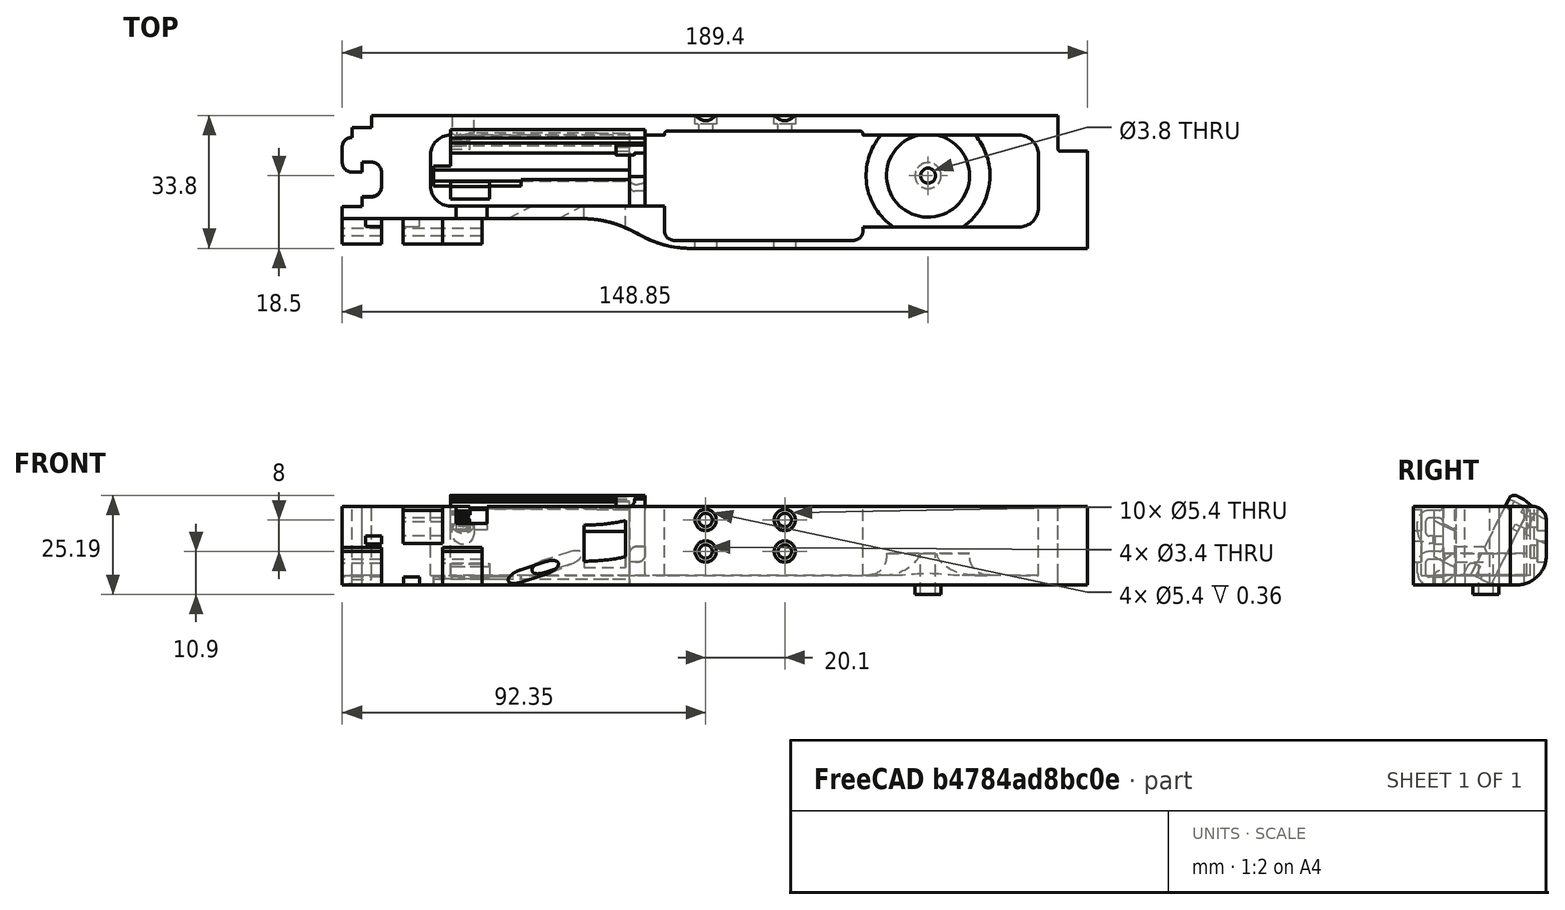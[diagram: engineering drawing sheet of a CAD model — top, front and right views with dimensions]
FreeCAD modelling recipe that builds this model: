
FCSTD DOCUMENT  (FreeCAD 0.19R0.19.2)
Label: rightSideV1_0
License: All rights reserved
LicenseURL: http://en.wikipedia.org/wiki/All_rights_reserved
objects: Sketcher::SketchObject×44, Part::Extrusion×35, Part::MultiFuse×23, Part::Box×18, Part::Cut×15, Part::Fillet×13, App::MeasureDistance×10, Part::Cylinder×4, Part::Revolution×1, Mesh::Feature×1
note: 153 computed .brp shape members not serialized (recipe doc carries the construction recipe); baked Part::Feature solids carry a one-line shape summary decoded from their .brp

FEATURE [Sketcher::SketchObject] Sketch
  FullyConstrained = true
  sketch-geometry (36):
    g0: LineSegment StartX=0 StartY=0 StartZ=0 EndX=154.4 EndY=0 EndZ=0
    g1: LineSegment StartX=154.4 StartY=0 StartZ=0 EndX=154.4 EndY=-7.6 EndZ=0
    g2: LineSegment StartX=32.5209 StartY=-26.2 StartZ=0 EndX=-7.5 EndY=-26.2 EndZ=0
    g3-g7: Circle x5 (B-spline internal-alignment scaffolding for g8; pole/knot coordinates omitted)
    g8: BSplineCurve PolesCount=5 KnotsCount=3 Degree=3 IsPeriodic=0
    g9: GeomPoint X=61.85 Y=-33.8 Z=0
    g10: GeomPoint X=47.185 Y=-29.9 Z=0
    g11: GeomPoint X=32.5209 Y=-26.2 Z=0
    g12: Circle CenterX=121.35 CenterY=-14.3 CenterZ=0 NormalX=0 NormalY=0 NormalZ=1 AngleXU=0 Radius=3.25
    g13: LineSegment StartX=-7.5 StartY=-26.2 StartZ=0 EndX=-27.5 EndY=-26.2 EndZ=0
    g14: LineSegment StartX=-20 StartY=0 StartZ=0 EndX=0 EndY=0 EndZ=0
    g15: LineSegment StartX=-25 StartY=-3.1 StartZ=0 EndX=-20 EndY=-3.1 EndZ=0
    g16: LineSegment StartX=-25 StartY=-3.1 StartZ=0 EndX=-25 EndY=-5.6 EndZ=0
    g17: LineSegment StartX=-27.5 StartY=-8.1 StartZ=0 EndX=-27.5 EndY=-11.85 EndZ=0
    g18: ArcOfCircle CenterX=-25 CenterY=-8.1 CenterZ=0 NormalX=0 NormalY=0 NormalZ=1 AngleXU=0 Radius=2.5 StartAngle=1.5708 EndAngle=3.14159
    g19: LineSegment StartX=-25 StartY=-14.35 StartZ=0 EndX=-22.5 EndY=-14.35 EndZ=0
    g20: ArcOfCircle CenterX=-25 CenterY=-11.85 CenterZ=0 NormalX=0 NormalY=0 NormalZ=1 AngleXU=0 Radius=2.5 StartAngle=3.14159 EndAngle=4.71239
    g21: LineSegment StartX=-22.5 StartY=-14.35 StartZ=0 EndX=-22.5 EndY=-11.85 EndZ=0
    g22: LineSegment StartX=-22.5 StartY=-11.85 StartZ=0 EndX=-20 EndY=-11.85 EndZ=0
    g23: ArcOfCircle CenterX=-20 CenterY=-14.35 CenterZ=0 NormalX=0 NormalY=0 NormalZ=1 AngleXU=0 Radius=2.5 StartAngle=8e-16 EndAngle=1.5708
    g24: LineSegment StartX=-17.5 StartY=-14.35 StartZ=0 EndX=-17.5 EndY=-18.1 EndZ=0
    g25: ArcOfCircle CenterX=-20 CenterY=-18.1 CenterZ=0 NormalX=0 NormalY=0 NormalZ=1 AngleXU=0 Radius=2.5 StartAngle=4.71239 EndAngle=6.28319
    g26: LineSegment StartX=-22.5 StartY=-20.6 StartZ=0 EndX=-20 EndY=-20.6 EndZ=0
    g27: LineSegment StartX=-22.5 StartY=-20.6 StartZ=0 EndX=-22.5 EndY=-23.1 EndZ=0
    g28: LineSegment StartX=-27.5 StartY=-23.1 StartZ=0 EndX=-22.5 EndY=-23.1 EndZ=0
    g29: LineSegment StartX=-20 StartY=-3.1 StartZ=0 EndX=-20 EndY=0 EndZ=0
    g30: LineSegment StartX=-27.5 StartY=-23.1 StartZ=0 EndX=-27.5 EndY=-26.2 EndZ=0
    g31: LineSegment StartX=154.4 StartY=-7.6 StartZ=0 EndX=154.4 EndY=-8.6 EndZ=0
    g32: ArcOfCircle CenterX=154.9 CenterY=-8.6 CenterZ=0 NormalX=0 NormalY=0 NormalZ=1 AngleXU=0 Radius=0.5 StartAngle=3.14159 EndAngle=4.71239
    g33: LineSegment StartX=154.9 StartY=-9.1 StartZ=0 EndX=161.9 EndY=-9.1 EndZ=0
    g34: LineSegment StartX=161.9 StartY=-9.1 StartZ=0 EndX=161.9 EndY=-33.8 EndZ=0
    g35: LineSegment StartX=161.9 StartY=-33.8 StartZ=0 EndX=61.85 EndY=-33.8 EndZ=0
  constraints (72):
    c: PointOnObject(g0,g-2)
    c: Horizontal(g0)
    c: Distance(g0) = 154.4
    c: DistanceY(g-1,g0) = 0
    c: Vertical(g1)
    c: Distance(g1) = 7.6
    c: Coincident(g1,g0)
    c: Horizontal(g2)
    c: Block(g2)
    c: Weight(g3) = 1
    c: Coincident(g8,g2)
    c: InternalAlignment(g3-g7 -> g8) x5
    c: InternalAlignment(g9,g8)
    c: InternalAlignment(g10,g8)
    c: InternalAlignment(g11,g8)
    c: Block(g12)
    c: Coincident(g13,g2)
    c: Horizontal(g13)
    c: Distance(g13) = 20
    c: Horizontal(g14)
    c: Distance(g14) = 20
    c: Coincident(g14,g0)
    c: Horizontal(g15)
    c: Vertical(g16)
    c: Coincident(g16,g15)
    c: Vertical(g17)
    c: Coincident(g18,g16)
    c: Block(g18)
    c: Coincident(g17,g18)
    c: Horizontal(g19)
    c: Coincident(g20,g17)
    c: Block(g20)
    c: Block(g19)
    c: Vertical(g21)
    c: Coincident(g21,g19)
    c: Horizontal(g22)
    c: Coincident(g22,g21)
    c: Coincident(g23,g22)
    c: Vertical(g24)
    c: Block(g23)
    c: Coincident(g24,g23)
    c: Coincident(g25,g24)
    c: Block(g25)
    c: Horizontal(g26)
    c: Coincident(g26,g25)
    c: Vertical(g27)
    c: Coincident(g27,g26)
    c: Horizontal(g28)
    c: Coincident(g28,g27)
    c: Block(g15)
    c: Block(g28)
    c: Coincident(g29,g15)
    c: Coincident(g29,g14)
    c: Vertical(g29)
    c: Coincident(g30,g28)
    c: Coincident(g30,g13)
    c: Vertical(g30)
    c: Vertical(g31)
    c: Distance(g31) = 1
    c: Coincident(g31,g1)
    c: Coincident(g32,g31)
    c: Block(g32)
    c: Coincident(g33,g32)
    c: Horizontal(g33)
    c: Coincident(g34,g33)
    c: Vertical(g34)
    c: Block(g34)
    c: Coincident(g35,g34)
    c: Horizontal(g35)
    c: Block(g35)
    c: Coincident(g8,g35)
    c: Block(g8)
FEATURE [Part::Extrusion] Extrude  label="mainBodyBaseExtrude"
  Base = -> Sketch
  Dir = (0,0,1)
  DirMode = 2
  FaceMakerClass = Part::FaceMakerBullseye
  LengthFwd = 2.4
  LengthRev = 0
  Solid = true
  Symmetric = false
FEATURE [Sketcher::SketchObject] Sketch001
  FullyConstrained = true
  sketch-geometry (75):
    g0: ArcOfCircle CenterX=144.4 CenterY=-10 CenterZ=0 NormalX=0 NormalY=0 NormalZ=1 AngleXU=0 Radius=5 StartAngle=4.345e-13 EndAngle=1.5708
    g1: LineSegment StartX=32.5209 StartY=-26.2 StartZ=0 EndX=-7.49911 EndY=-26.2 EndZ=0
    g2: LineSegment StartX=0 StartY=0 StartZ=0 EndX=154.4 EndY=0 EndZ=0
    g3-g7: Circle x5 (B-spline internal-alignment scaffolding for g8; pole/knot coordinates omitted)
    g8: BSplineCurve PolesCount=5 KnotsCount=3 Degree=3 IsPeriodic=0
    g9: GeomPoint X=61.85 Y=-33.8 Z=0
    g10: GeomPoint X=47.1857 Y=-29.9 Z=0
    g11: GeomPoint X=32.5209 Y=-26.2 Z=0
    g12: LineSegment StartX=154.4 StartY=0 StartZ=0 EndX=154.4 EndY=-7.6 EndZ=0
    g13: LineSegment StartX=20 StartY=-5 StartZ=0 EndX=54.35 EndY=-5 EndZ=0
    g14: LineSegment StartX=104.85 StartY=-5 StartZ=0 EndX=144.4 EndY=-5 EndZ=0
    g15: LineSegment StartX=54.35 StartY=-23 StartZ=0 EndX=20 EndY=-23 EndZ=0
    g16: LineSegment StartX=-27.4991 StartY=-26.2 StartZ=0 EndX=-7.49911 EndY=-26.2 EndZ=0
    g17: LineSegment StartX=-20 StartY=0 StartZ=0 EndX=0 EndY=0 EndZ=0
    g18: LineSegment StartX=-27.4991 StartY=-23.2 StartZ=0 EndX=-22.5 EndY=-23.2 EndZ=0
    g19: LineSegment StartX=-22.5 StartY=-20.7 StartZ=0 EndX=-22.5 EndY=-23.2 EndZ=0
    g20: LineSegment StartX=-22.5 StartY=-20.7 StartZ=0 EndX=-20 EndY=-20.7 EndZ=0
    g21: ArcOfCircle CenterX=-20 CenterY=-18.2 CenterZ=0 NormalX=0 NormalY=0 NormalZ=1 AngleXU=0 Radius=2.5 StartAngle=4.71239 EndAngle=6.28319
    g22: LineSegment StartX=-17.5 StartY=-14.4 StartZ=0 EndX=-17.5 EndY=-18.2 EndZ=0
    g23: ArcOfCircle CenterX=-20 CenterY=-14.4 CenterZ=0 NormalX=0 NormalY=0 NormalZ=1 AngleXU=0 Radius=2.5 StartAngle=9e-16 EndAngle=1.5708
    g24: LineSegment StartX=-22.5 StartY=-11.9 StartZ=0 EndX=-20 EndY=-11.9 EndZ=0
    g25: LineSegment StartX=-22.5 StartY=-14.4 StartZ=0 EndX=-22.5 EndY=-11.9 EndZ=0
    g26: LineSegment StartX=-25 StartY=-14.4 StartZ=0 EndX=-22.5 EndY=-14.4 EndZ=0
    g27: ArcOfCircle CenterX=-25 CenterY=-11.9 CenterZ=0 NormalX=0 NormalY=0 NormalZ=1 AngleXU=0 Radius=2.5 StartAngle=3.14159 EndAngle=4.71239
    g28: LineSegment StartX=-27.5 StartY=-8.1 StartZ=0 EndX=-27.5 EndY=-11.9 EndZ=0
    g29: ArcOfCircle CenterX=-25 CenterY=-8.1 CenterZ=0 NormalX=0 NormalY=0 NormalZ=1 AngleXU=0 Radius=2.5 StartAngle=1.5708 EndAngle=3.14159
    g30: LineSegment StartX=-25 StartY=-3.1 StartZ=0 EndX=-25 EndY=-5.6 EndZ=0
    g31: LineSegment StartX=-20 StartY=-3.1 StartZ=0 EndX=-25 EndY=-3.1 EndZ=0
    g32: LineSegment StartX=-20 StartY=0 StartZ=0 EndX=-20 EndY=-3.1 EndZ=0
    g33: LineSegment StartX=-27.4991 StartY=-26.2 StartZ=0 EndX=-27.4991 EndY=-23.2 EndZ=0
    g34: LineSegment StartX=4.09e-14 StartY=-5 StartZ=0 EndX=20 EndY=-5 EndZ=0
    g35: ArcOfCircle CenterX=7.1e-15 CenterY=-18 CenterZ=0 NormalX=0 NormalY=0 NormalZ=1 AngleXU=0 Radius=5 StartAngle=3.14159 EndAngle=4.71239
    g36: ArcOfCircle CenterX=4.26e-14 CenterY=-10 CenterZ=0 NormalX=0 NormalY=0 NormalZ=1 AngleXU=0 Radius=5 StartAngle=1.5708 EndAngle=3.14159
    g37: LineSegment StartX=-5 StartY=-18 StartZ=0 EndX=-5 EndY=-10 EndZ=0
    g38: LineSegment StartX=6.2e-15 StartY=-23 StartZ=0 EndX=20 EndY=-23 EndZ=0
    g39: LineSegment StartX=154.4 StartY=-7.6 StartZ=0 EndX=154.4 EndY=-8.6 EndZ=0
    g40: LineSegment StartX=154.9 StartY=-9.1 StartZ=0 EndX=161.9 EndY=-9.1 EndZ=0
    g41: ArcOfCircle CenterX=154.9 CenterY=-8.6 CenterZ=0 NormalX=0 NormalY=0 NormalZ=1 AngleXU=0 Radius=0.5 StartAngle=3.14159 EndAngle=4.71299
    g42: LineSegment StartX=104.85 StartY=-28.3916 StartZ=0 EndX=144.408 EndY=-28.3916 EndZ=0
    g43: LineSegment StartX=149.4 StartY=-10 StartZ=0 EndX=149.4 EndY=-23.4 EndZ=0
    g44: ArcOfCircle CenterX=144.408 CenterY=-23.4 CenterZ=0 NormalX=0 NormalY=0 NormalZ=1 AngleXU=0 Radius=4.99164 StartAngle=4.71239 EndAngle=6.28319
    g45: LineSegment StartX=104.85 StartY=-28.3916 StartZ=0 EndX=104.85 EndY=-28.7833 EndZ=0
    g46: LineSegment StartX=54.35 StartY=-28.7916 StartZ=0 EndX=54.35 EndY=-23 EndZ=0
    g47: LineSegment StartX=161.9 StartY=-33.8 StartZ=0 EndX=161.9 EndY=-9.1 EndZ=0
    g48: LineSegment StartX=61.85 StartY=-33.8 StartZ=0 EndX=161.9 EndY=-33.8 EndZ=0
    g49: Circle CenterX=54.35 CenterY=-28.7916 CenterZ=0 NormalX=0 NormalY=0 NormalZ=1 AngleXU=0 Radius=1
    g50: Circle CenterX=54.35 CenterY=-31.7916 CenterZ=0 NormalX=0 NormalY=0 NormalZ=1 AngleXU=0 Radius=1
    g51: Circle CenterX=57.35 CenterY=-31.7916 CenterZ=0 NormalX=0 NormalY=0 NormalZ=1 AngleXU=0 Radius=1
    g52: BSplineCurve PolesCount=3 KnotsCount=2 Degree=2 IsPeriodic=0
    g53: GeomPoint X=54.35 Y=-28.7916 Z=0
    g54: GeomPoint X=57.35 Y=-31.7916 Z=0
    g55: Circle CenterX=104.85 CenterY=-28.7833 CenterZ=0 NormalX=0 NormalY=0 NormalZ=1 AngleXU=0 Radius=1
    g56: Circle CenterX=104.85 CenterY=-31.7916 CenterZ=0 NormalX=0 NormalY=0 NormalZ=1 AngleXU=0 Radius=1
    g57: Circle CenterX=101.85 CenterY=-31.7916 CenterZ=0 NormalX=0 NormalY=0 NormalZ=1 AngleXU=0 Radius=1
    g58: BSplineCurve PolesCount=3 KnotsCount=2 Degree=2 IsPeriodic=0
    g59: GeomPoint X=104.85 Y=-28.7833 Z=0
    g60: GeomPoint X=101.85 Y=-31.7916 Z=0
    g61: LineSegment StartX=57.35 StartY=-31.7916 StartZ=0 EndX=101.85 EndY=-31.7916 EndZ=0
    g62: Circle CenterX=54.35 CenterY=-5 CenterZ=0 NormalX=0 NormalY=0 NormalZ=1 AngleXU=0 Radius=1
    g63: Circle CenterX=54.35 CenterY=-4 CenterZ=0 NormalX=0 NormalY=0 NormalZ=1 AngleXU=0 Radius=1
    g64: Circle CenterX=55.15 CenterY=-4 CenterZ=0 NormalX=0 NormalY=0 NormalZ=1 AngleXU=0 Radius=1
    g65: BSplineCurve PolesCount=3 KnotsCount=2 Degree=2 IsPeriodic=0
    g66: GeomPoint X=54.35 Y=-5 Z=0
    g67: GeomPoint X=55.15 Y=-4 Z=0
    g68: Circle CenterX=104.85 CenterY=-5 CenterZ=0 NormalX=0 NormalY=0 NormalZ=1 AngleXU=0 Radius=1
    g69: Circle CenterX=104.85 CenterY=-4 CenterZ=0 NormalX=0 NormalY=0 NormalZ=1 AngleXU=0 Radius=1
    g70: Circle CenterX=104.05 CenterY=-4 CenterZ=0 NormalX=0 NormalY=0 NormalZ=1 AngleXU=0 Radius=1
    g71: BSplineCurve PolesCount=3 KnotsCount=2 Degree=2 IsPeriodic=0
    g72: GeomPoint X=104.85 Y=-5 Z=0
    g73: GeomPoint X=104.05 Y=-4 Z=0
    g74: LineSegment StartX=104.05 StartY=-4 StartZ=0 EndX=55.15 EndY=-4 EndZ=0
  constraints (156):
    c: PointOnObject(g2,g-2)
    c: DistanceY(g-1,g2) = 0
    c: Block(g0)
    c: Horizontal(g1)
    c: Distance(g1) = 40.02
    c: Horizontal(g2)
    c: Block(g2)
    c: Weight(g3) = 1
    c: Equal(g3, g4-g7) x4
    c: Coincident(g8,g1)
    c: InternalAlignment(g3-g7 -> g8) x5
    c: InternalAlignment(g9,g8)
    c: InternalAlignment(g10,g8)
    c: InternalAlignment(g11,g8)
    c: Vertical(g12)
    c: Coincident(g12,g2)
    c: Distance(g12) = 7.6
    c: Block(g12)
    c: Horizontal(g13)
    c: Coincident(g14,g0)
    c: Horizontal(g14)
    c: Horizontal(g15)
    c: Horizontal(g16)
    c: Distance(g16) = 20
    c: Coincident(g1,g16)
    c: Horizontal(g17)
    c: Distance(g17) = 20
    c: Coincident(g17,g2)
    c: Horizontal(g31)
    c: Vertical(g30)
    c: Coincident(g29,g30)
    c: Vertical(g28)
    c: Block(g29)
    c: Coincident(g27,g28)
    c: Block(g27)
    c: Horizontal(g26)
    c: Coincident(g26,g27)
    c: Vertical(g25)
    c: Coincident(g25,g26)
    c: Horizontal(g24)
    c: Coincident(g23,g24)
    c: Block(g23)
    c: Vertical(g22)
    c: Coincident(g21,g22)
    c: Block(g21)
    c: Horizontal(g20)
    c: Coincident(g20,g21)
    c: Vertical(g19)
    c: Coincident(g19,g20)
    c: Horizontal(g18)
    c: Coincident(g18,g19)
    c: Coincident(g32,g17)
    c: Coincident(g32,g31)
    c: Vertical(g32)
    c: Coincident(g33,g16)
    c: Coincident(g33,g18)
    c: Vertical(g33)
    c: Block(g33)
    c: Block(g18)
    c: Block(g22)
    c: Block(g26)
    c: Block(g25)
    c: Block(g24)
    c: Block(g28)
    c: Block(g31)
    c: Block(g30)
    c: Horizontal(g34)
    c: Distance(g34) = 20
    c: Block(g35)
    c: Block(g36)
    c: Coincident(g37,g35)
    c: Coincident(g37,g36)
    c: Vertical(g37)
    c: Coincident(g38,g35)
    c: Coincident(g38,g15)
    c: Horizontal(g38)
    c: Block(g38)
    c: Block(g34)
    c: Block(g13)
    c: Vertical(g39)
    c: Distance(g39) = 1
    c: Coincident(g39,g12)
    c: Horizontal(g40)
    c: Coincident(g41,g39)
    c: Coincident(g41,g40)
    c: Block(g39)
    c: Block(g41)
    c: Horizontal(g42)
    c: Vertical(g43)
    c: Distance(g43) = 13.4
    c: Coincident(g43,g0)
    c: Block(g42)
    c: Block(g43)
    c: Coincident(g44,g43)
    c: Coincident(g44,g42)
    c: Block(g44)
    c: Distance(g15) = 34.35
    c: Coincident(g45,g42)
    c: Vertical(g45)
    c: Coincident(g46,g15)
    c: Vertical(g46)
    c: Coincident(g47,g40)
    c: Vertical(g47)
    c: Block(g47)
    c: Coincident(g48,g47)
    c: Horizontal(g48)
    c: Block(g48)
    c: Coincident(g8,g48)
    c: Block(g8)
    c: Coincident(g52,g46)
    c: Weight(g49) = 1
    c: Equal(g49,g50)
    c: Equal(g49,g51)
    c: InternalAlignment(g49,g52)
    c: InternalAlignment(g50,g52)
    c: InternalAlignment(g51,g52)
    c: InternalAlignment(g53,g52)
    c: InternalAlignment(g54,g52)
    c: Coincident(g58,g45)
    c: Weight(g55) = 1
    c: Equal(g55,g56)
    c: Equal(g55,g57)
    c: InternalAlignment(g55,g58)
    c: InternalAlignment(g56,g58)
    c: InternalAlignment(g57,g58)
    c: InternalAlignment(g59,g58)
    c: InternalAlignment(g60,g58)
    c: Block(g58)
    c: Block(g52)
    c: Coincident(g61,g52)
    c: Coincident(g61,g58)
    c: Horizontal(g61)
    c: Block(g14)
    c: Coincident(g65,g13)
    c: Weight(g62) = 1
    c: Equal(g62,g63)
    c: Equal(g62,g64)
    c: InternalAlignment(g62,g65)
    c: InternalAlignment(g63,g65)
    c: InternalAlignment(g64,g65)
    c: InternalAlignment(g66,g65)
    c: InternalAlignment(g67,g65)
    c: Block(g65)
    c: Coincident(g71,g14)
    c: Weight(g68) = 1
    c: Equal(g68,g69)
    c: Equal(g68,g70)
    c: InternalAlignment(g68,g71)
    c: InternalAlignment(g69,g71)
    c: InternalAlignment(g70,g71)
    c: InternalAlignment(g72,g71)
    c: InternalAlignment(g73,g71)
    c: Block(g71)
    c: Coincident(g74,g71)
    c: Coincident(g74,g65)
    c: Horizontal(g74)
FEATURE [Sketcher::SketchObject] Sketch005
  FullyConstrained = true
  Placement = pos=(0,0,0) rot=(1,0,0;1.5708rad)
  sketch-geometry (4):
    g0: Circle CenterX=84.95 CenterY=16.5 CenterZ=0 NormalX=0 NormalY=0 NormalZ=1 AngleXU=0 Radius=1.7
    g1: Circle CenterX=84.95 CenterY=8.5 CenterZ=0 NormalX=0 NormalY=0 NormalZ=1 AngleXU=0 Radius=1.7
    g2: Circle CenterX=64.85 CenterY=8.5 CenterZ=0 NormalX=0 NormalY=0 NormalZ=1 AngleXU=0 Radius=1.7
    g3: Circle CenterX=64.85 CenterY=16.5 CenterZ=0 NormalX=0 NormalY=0 NormalZ=1 AngleXU=0 Radius=1.7
  constraints (4):
    c: Block(g0)
    c: Block(g1)
    c: Block(g2)
    c: Block(g3)
FEATURE [Part::Extrusion] Extrude004  label="removeFromMainBodyToCreateScrewHolesForSolenoidExtrude004"
  Base = -> Sketch005
  Dir = (0,-1,1.1e-15)
  DirMode = 2
  FaceMakerClass = Part::FaceMakerBullseye
  LengthFwd = 10
  LengthRev = 0
  Solid = true
  Symmetric = false
FEATURE [Sketcher::SketchObject] Sketch004
  FullyConstrained = true
  Placement = pos=(0,0,0) rot=(1,0,0;1.5708rad)
  sketch-geometry (12):
    g0: LineSegment StartX=15.75 StartY=2.5 StartZ=0 EndX=15.75 EndY=0 EndZ=0
    g1: Circle CenterX=15.75 CenterY=2.5 CenterZ=0 NormalX=0 NormalY=0 NormalZ=1 AngleXU=0 Radius=1
    g2: Circle CenterX=10.55 CenterY=2.5 CenterZ=0 NormalX=0 NormalY=0 NormalZ=1 AngleXU=0 Radius=1
    g3: Circle CenterX=10.55 CenterY=8 CenterZ=0 NormalX=0 NormalY=0 NormalZ=1 AngleXU=0 Radius=1
    g4: BSplineCurve PolesCount=3 KnotsCount=2 Degree=2 IsPeriodic=0
    g5: GeomPoint X=15.75 Y=2.5 Z=0
    g6: GeomPoint X=10.55 Y=8 Z=0
    g7: LineSegment StartX=1.9 StartY=8 StartZ=0 EndX=10.55 EndY=8 EndZ=0
    g8: LineSegment StartX=1.9 StartY=-2.4 StartZ=0 EndX=1.9 EndY=8 EndZ=0
    g9: LineSegment StartX=3.30092 StartY=-2.4 StartZ=0 EndX=3.30092 EndY=0 EndZ=0
    g10: LineSegment StartX=15.75 StartY=0 StartZ=0 EndX=3.30092 EndY=0 EndZ=0
    g11: LineSegment StartX=3.30092 StartY=-2.4 StartZ=0 EndX=1.9 EndY=-2.4 EndZ=0
  constraints (26):
    c: Vertical(g0)
    c: Distance(g0) = 2.5
    c: Coincident(g4,g0)
    c: Weight(g1) = 1
    c: Equal(g1,g2)
    c: Equal(g1,g3)
    c: InternalAlignment(g1,g4)
    c: InternalAlignment(g2,g4)
    c: InternalAlignment(g3,g4)
    c: InternalAlignment(g5,g4)
    c: InternalAlignment(g6,g4)
    c: Block(g4)
    c: Coincident(g7,g4)
    c: Horizontal(g7)
    c: Vertical(g8)
    c: Coincident(g8,g7)
    c: Block(g8)
    c: Vertical(g9)
    c: Coincident(g10,g0)
    c: PointOnObject(g10,g-1)
    c: Horizontal(g10)
    c: Coincident(g10,g9)
    c: Block(g9)
    c: Coincident(g11,g9)
    c: Coincident(g11,g8)
    c: Horizontal(g11)
FEATURE [Sketcher::SketchObject] Sketch007
  FullyConstrained = true
  Placement = pos=(0,-14.3,2.37) rot=(-1,0,0;2.03453rad)
  sketch-geometry (6):
    g0: LineSegment StartX=0 StartY=0 StartZ=0 EndX=45.5 EndY=0 EndZ=0
    g1: LineSegment StartX=0 StartY=0 StartZ=0 EndX=0 EndY=-21.2 EndZ=0
    g2: LineSegment StartX=45.5 StartY=0 StartZ=0 EndX=49.5 EndY=0 EndZ=0
    g3: LineSegment StartX=49.5 StartY=0 StartZ=0 EndX=49.5 EndY=-21.2 EndZ=0
    g4: LineSegment StartX=49.5 StartY=-21.2 StartZ=0 EndX=0 EndY=-21.2 EndZ=0
    g5: Circle CenterX=3.25 CenterY=-18.05 CenterZ=0 NormalX=0 NormalY=0 NormalZ=1 AngleXU=0 Radius=1.6
  constraints (15):
    c: Coincident(g0,g-1)
    c: Horizontal(g0)
    c: Distance(g0) = 45.5
    c: Coincident(g1,g0)
    c: Vertical(g1)
    c: Horizontal(g2)
    c: Distance(g2) = 4
    c: Coincident(g2,g0)
    c: Coincident(g3,g2)
    c: Vertical(g3)
    c: Block(g3)
    c: Coincident(g4,g3)
    c: Horizontal(g4)
    c: Coincident(g4,g1)
    c: Block(g5)
FEATURE [Part::Extrusion] Extrude005  label="solenoidDriverHolderExtrude005"
  Base = -> Sketch007
  Dir = (0,0.894389,-0.447291)
  DirMode = 2
  FaceMakerClass = Part::FaceMakerBullseye
  LengthFwd = 10
  LengthRev = 0
  Placement = pos=(0,0,-2) rot=(0,0,1;0rad)
  Solid = true
  Symmetric = false
FEATURE [Sketcher::SketchObject] Sketch008
  FullyConstrained = false
  Placement = pos=(0,-4.3,-2.6) rot=(-1,0,0;2.03453rad)
  sketch-geometry (1):
    g0: Circle CenterX=42.25 CenterY=-3.15 CenterZ=0 NormalX=0 NormalY=0 NormalZ=1 AngleXU=0 Radius=4.5
FEATURE [Sketcher::SketchObject] Sketch009
  FullyConstrained = true
  Placement = pos=(0,-4.3,-2.6) rot=(-1,0,0;2.03453rad)
  sketch-geometry (1):
    g0: Circle CenterX=3.25 CenterY=-18.0217 CenterZ=0 NormalX=0 NormalY=0 NormalZ=1 AngleXU=0 Radius=2.8
  constraints (1):
    c: Block(g0)
FEATURE [Sketcher::SketchObject] Sketch010
  FullyConstrained = true
  Placement = pos=(0,-14.3,2.37) rot=(-1,0,0;2.03453rad)
  sketch-geometry (1):
    g0: Circle CenterX=3.25 CenterY=-18.05 CenterZ=0 NormalX=0 NormalY=0 NormalZ=1 AngleXU=0 Radius=1.6
  constraints (1):
    c: Block(g0)
FEATURE [Part::Extrusion] Extrude008  label="removeFromScrewHole3"
  Base = -> Sketch010
  Dir = (0,0.894389,-0.447291)
  DirMode = 2
  FaceMakerClass = Part::FaceMakerBullseye
  LengthFwd = -25
  LengthRev = 0
  Placement = pos=(0,4,-4) rot=(0,0,1;0rad)
  Solid = true
  Symmetric = false
FEATURE [Sketcher::SketchObject] Sketch011
  FullyConstrained = true
  Placement = pos=(0,-14.3,2.37) rot=(-1,0,0;2.03453rad)
  sketch-geometry (4):
    g0: LineSegment StartX=49.5 StartY=-21.2 StartZ=0 EndX=49.5 EndY=-22.8 EndZ=0
    g1: LineSegment StartX=49.5 StartY=-22.8 StartZ=0 EndX=0.002238 EndY=-22.8 EndZ=0
    g2: LineSegment StartX=0.002238 StartY=-21.2 StartZ=0 EndX=0.002238 EndY=-22.8 EndZ=0
    g3: LineSegment StartX=49.5 StartY=-21.2 StartZ=0 EndX=0.002238 EndY=-21.2 EndZ=0
  constraints (10):
    c: Vertical(g0)
    c: Distance(g0) = 1.6
    c: Coincident(g1,g0)
    c: Horizontal(g1)
    c: Vertical(g2)
    c: Coincident(g2,g1)
    c: Coincident(g3,g0)
    c: Coincident(g3,g2)
    c: Horizontal(g3)
    c: Block(g3)
FEATURE [Part::Extrusion] Extrude009  label="solenoidDriverTopLipFront"
  Base = -> Sketch011
  Dir = (0,0.894389,-0.447291)
  DirMode = 2
  FaceMakerClass = Part::FaceMakerBullseye
  LengthFwd = -2
  LengthRev = 0
  Placement = pos=(0,-2.9,-0.35) rot=(0,0,1;0rad)
  Solid = true
  Symmetric = false
FEATURE [Sketcher::SketchObject] Sketch012
  FullyConstrained = true
  Placement = pos=(0,-14.3,2.37) rot=(-1,0,0;2.03453rad)
  sketch-geometry (4):
    g0: LineSegment StartX=49.5 StartY=-21.2 StartZ=0 EndX=49.5 EndY=-22.8 EndZ=0
    g1: LineSegment StartX=49.5 StartY=-22.8 StartZ=0 EndX=0.002238 EndY=-22.8 EndZ=0
    g2: LineSegment StartX=0.002238 StartY=-21.2 StartZ=0 EndX=0.002238 EndY=-22.8 EndZ=0
    g3: LineSegment StartX=49.5 StartY=-21.2 StartZ=0 EndX=0.002238 EndY=-21.2 EndZ=0
  constraints (10):
    c: Vertical(g0)
    c: Distance(g0) = 1.6
    c: Coincident(g1,g0)
    c: Horizontal(g1)
    c: Vertical(g2)
    c: Coincident(g2,g1)
    c: Coincident(g3,g0)
    c: Coincident(g3,g2)
    c: Horizontal(g3)
    c: Block(g3)
FEATURE [Part::Extrusion] Extrude010  label="solenoidDriverTopLipLowerExtrude010"
  Base = -> Sketch012
  Dir = (0,0.894389,-0.447291)
  DirMode = 2
  FaceMakerClass = Part::FaceMakerBullseye
  LengthFwd = 5.05
  LengthRev = 0
  Solid = true
  Symmetric = false
FEATURE [Sketcher::SketchObject] Sketch015
  FullyConstrained = true
  Placement = pos=(0,-14.3,2.37) rot=(-1,0,0;2.03453rad)
  sketch-geometry (4):
    g0: LineSegment StartX=0 StartY=1.5 StartZ=0 EndX=0 EndY=0 EndZ=0
    g1: LineSegment StartX=0 StartY=1.5 StartZ=0 EndX=5 EndY=1.5 EndZ=0
    g2: LineSegment StartX=5 StartY=1.5 StartZ=0 EndX=5 EndY=0 EndZ=0
    g3: LineSegment StartX=0 StartY=0 StartZ=0 EndX=5 EndY=0 EndZ=0
  constraints (13):
    c: Vertical(g0)
    c: Distance(g0) = 1.5
    c: Horizontal(g1)
    c: Distance(g1) = 5
    c: Coincident(g1,g0)
    c: Vertical(g2)
    c: Distance(g2) = 1.5
    c: Coincident(g2,g1)
    c: Block(g1)
    c: Block(g2)
    c: Block(g0)
    c: Coincident(g3,g0)
    c: Coincident(g3,g2)
FEATURE [Part::Extrusion] Extrude013  label="solenoidDriverBottomLipTopExtrude012"
  Base = -> Sketch015
  Dir = (0,0.894389,-0.447291)
  DirMode = 2
  FaceMakerClass = Part::FaceMakerBullseye
  LengthFwd = -6.5
  LengthRev = 0
  Placement = pos=(0,-14.15,19.65) rot=(1,0,0;1.5708rad)
  Solid = true
  Symmetric = false
FEATURE [Sketcher::SketchObject] Sketch016
  FullyConstrained = true
  Placement = pos=(0,0,0) rot=(1,0,0;1.5708rad)
  sketch-geometry (4):
    g0: Circle CenterX=84.15 CenterY=16.5 CenterZ=0 NormalX=0 NormalY=0 NormalZ=1 AngleXU=0 Radius=2.7
    g1: Circle CenterX=64.05 CenterY=16.5 CenterZ=0 NormalX=0 NormalY=0 NormalZ=1 AngleXU=0 Radius=2.7
    g2: Circle CenterX=64.05 CenterY=8.5 CenterZ=0 NormalX=0 NormalY=0 NormalZ=1 AngleXU=0 Radius=2.7
    g3: Circle CenterX=84.15 CenterY=8.5 CenterZ=0 NormalX=0 NormalY=0 NormalZ=1 AngleXU=0 Radius=2.7
  constraints (4):
    c: Block(g0)
    c: Block(g1)
    c: Block(g3)
    c: Block(g2)
FEATURE [Part::Extrusion] Extrude014  label="removeFromMainBodyToCreateScrewHoleCounterSinks"
  Base = -> Sketch016
  Dir = (0,-1,1.1e-15)
  DirMode = 2
  FaceMakerClass = Part::FaceMakerBullseye
  LengthFwd = 1.9
  LengthRev = 0
  Placement = pos=(0.8,-0.36,0) rot=(0,0,1;0rad)
  Solid = true
  Symmetric = false
FEATURE [Part::Extrusion] Extrude015  label="removeFromScrewHole2Extrude007"
  Base = -> Sketch009
  Dir = (0,0.894389,-0.447291)
  DirMode = 2
  FaceMakerClass = Part::FaceMakerBullseye
  LengthFwd = 10
  LengthRev = 0
  Placement = pos=(0,-8,2) rot=(0,0,1;0rad)
  Solid = true
  Symmetric = false
FEATURE [Sketcher::SketchObject] Sketch017
  FullyConstrained = true
  Placement = pos=(0,-14.3,2.37) rot=(-1,0,0;2.03453rad)
  sketch-geometry (4):
    g0: LineSegment StartX=0 StartY=1.5 StartZ=0 EndX=0 EndY=0 EndZ=0
    g1: LineSegment StartX=0 StartY=1.5 StartZ=0 EndX=5 EndY=1.5 EndZ=0
    g2: LineSegment StartX=5 StartY=1.5 StartZ=0 EndX=5 EndY=0 EndZ=0
    g3: LineSegment StartX=0 StartY=0 StartZ=0 EndX=5 EndY=0 EndZ=0
  constraints (13):
    c: Vertical(g0)
    c: Distance(g0) = 1.5
    c: Horizontal(g1)
    c: Distance(g1) = 5
    c: Coincident(g1,g0)
    c: Vertical(g2)
    c: Distance(g2) = 1.5
    c: Coincident(g2,g1)
    c: Block(g1)
    c: Block(g2)
    c: Block(g0)
    c: Coincident(g3,g0)
    c: Coincident(g3,g2)
FEATURE [Part::Extrusion] Extrude016  label="solenoidDriverBottomLipTopExtrude013"
  Base = -> Sketch017
  Dir = (0,0.894389,-0.447291)
  DirMode = 2
  FaceMakerClass = Part::FaceMakerBullseye
  LengthFwd = -6.5
  LengthRev = 0
  Placement = pos=(0,-15.45,20.3) rot=(1,0,0;1.5708rad)
  Solid = true
  Symmetric = false
FEATURE [Part::Fillet] Fillet005  label="solenoidDriverBottomLipTopFillet005"
  Base = -> Extrude016
  Edges = 1 edges r=1.4: [Edge6]
FEATURE [Sketcher::SketchObject] Sketch018
  FullyConstrained = true
  Placement = pos=(38.5,-14.3,2.37) rot=(-1,0,0;2.03453rad)
  sketch-geometry (4):
    g0: LineSegment StartX=11 StartY=0 StartZ=0 EndX=11 EndY=1.5 EndZ=0
    g1: LineSegment StartX=11 StartY=0 StartZ=0 EndX=3.6 EndY=0 EndZ=0
    g2: LineSegment StartX=3.6 StartY=0 StartZ=0 EndX=3.6 EndY=1.5 EndZ=0
    g3: LineSegment StartX=11 StartY=1.5 StartZ=0 EndX=3.6 EndY=1.5 EndZ=0
  constraints (12):
    c: PointOnObject(g0,g-1)
    c: Vertical(g0)
    c: Distance(g0) = 1.5
    c: Horizontal(g1)
    c: Distance(g1) = 7.4
    c: Coincident(g1,g0)
    c: Block(g0)
    c: Coincident(g2,g1)
    c: Vertical(g2)
    c: Coincident(g3,g0)
    c: Horizontal(g3)
    c: Coincident(g2,g3)
FEATURE [Part::Extrusion] Extrude017
  Base = -> Sketch018
  Dir = (0,0.894389,-0.447291)
  DirMode = 2
  FaceMakerClass = Part::FaceMakerBullseye
  LengthFwd = 4
  LengthRev = 0
  Placement = pos=(0,-8.212,34.025) rot=(1,0,0;1.5708rad)
  Solid = true
  Symmetric = false
FEATURE [Sketcher::SketchObject] Sketch019
  FullyConstrained = true
  Placement = pos=(0,0,0) rot=(1,0,0;1.5708rad)
  sketch-geometry (4):
    g0: Circle CenterX=84.95 CenterY=8.5 CenterZ=0 NormalX=0 NormalY=0 NormalZ=1 AngleXU=0 Radius=2.7
    g1: Circle CenterX=64.85 CenterY=8.5 CenterZ=0 NormalX=0 NormalY=0 NormalZ=1 AngleXU=0 Radius=2.7
    g2: Circle CenterX=64.85 CenterY=16.5 CenterZ=0 NormalX=0 NormalY=0 NormalZ=1 AngleXU=0 Radius=2.7
    g3: Circle CenterX=84.95 CenterY=16.5 CenterZ=0 NormalX=0 NormalY=0 NormalZ=1 AngleXU=0 Radius=2.7
  constraints (4):
    c: Block(g3)
    c: Block(g2)
    c: Block(g0)
    c: Block(g1)
FEATURE [Part::Extrusion] Extrude019  label="removeSolenoidAdjusterHoles"
  Base = -> Sketch019
  Dir = (0,-1,1.1e-15)
  DirMode = 2
  FaceMakerClass = Part::FaceMakerBullseye
  LengthFwd = 6
  LengthRev = 0
  Placement = pos=(0,-30,0) rot=(0,0,1;0rad)
  Solid = true
  Symmetric = false
FEATURE [Sketcher::SketchObject] Sketch020
  FullyConstrained = true
  Placement = pos=(0,-14.3,2.37) rot=(-1,0,0;2.03453rad)
  sketch-geometry (6):
    g0: LineSegment StartX=45.5 StartY=-21.2 StartZ=0 EndX=49.5 EndY=-21.2 EndZ=0
    g1: LineSegment StartX=45.5 StartY=0 StartZ=0 EndX=49.5 EndY=0 EndZ=0
    g2: LineSegment StartX=49.5 StartY=0 StartZ=0 EndX=49.5 EndY=-21.2 EndZ=0
    g3: LineSegment StartX=4 StartY=0 StartZ=0 EndX=4 EndY=-21.2 EndZ=0
    g4: LineSegment StartX=45.5 StartY=-21.2 StartZ=0 EndX=4 EndY=-21.2 EndZ=0
    g5: LineSegment StartX=4 StartY=0 StartZ=0 EndX=45.5 EndY=0 EndZ=0
  constraints (16):
    c: Horizontal(g0)
    c: Distance(g0) = 4
    c: Horizontal(g1)
    c: Distance(g1) = 4
    c: Coincident(g2,g1)
    c: Coincident(g2,g0)
    c: Vertical(g2)
    c: Block(g2)
    c: Vertical(g3)
    c: Coincident(g4,g0)
    c: Horizontal(g4)
    c: Coincident(g4,g3)
    c: Coincident(g5,g1)
    c: Horizontal(g5)
    c: Block(g3)
    c: Block(g5)
FEATURE [Part::Box] Box  label="Cube"
  AttacherType = Attacher::AttachEngine3D
  Height = 10
  Length = 190
  Placement = pos=(-30,0,0) rot=(0,0,1;0rad)
  Width = 10
FEATURE [Part::Fillet] Fillet008
  Base = -> Box
  Edges = 1 edges r=7.5: [Edge11]
FEATURE [Part::Box] Box001  label="Cube001"
  AttacherType = Attacher::AttachEngine3D
  Height = 10
  Length = 190
  Placement = pos=(-35,0,0) rot=(0,0,1;0rad)
  Width = 10
FEATURE [Part::Cut] Cut  label="filletMain"
  Base = -> Box001
  Placement = pos=(0,-10,0) rot=(0,0,1;0rad)
  Tool = -> Fillet008
FEATURE [Part::Box] Box002  label="Cube002"
  AttacherType = Attacher::AttachEngine3D
  Height = 30
  Length = 190
  Placement = pos=(-20,0,0) rot=(0,0,1;0rad)
  Width = 10
FEATURE [Part::Box] Box003  label="Cube003"
  AttacherType = Attacher::AttachEngine3D
  Height = 10
  Length = 190
  Placement = pos=(-90,-50,-10) rot=(0,0,1;0rad)
  Width = 50
FEATURE [Sketcher::SketchObject] Sketch021
  FullyConstrained = true
  Placement = pos=(0,-14.3,2.37) rot=(-1,0,0;2.03453rad)
  sketch-geometry (6):
    g0: LineSegment StartX=41.65 StartY=-3.15 StartZ=0 EndX=38.95 EndY=-3.15 EndZ=0
    g1: LineSegment StartX=36.25 StartY=-3.15 StartZ=0 EndX=38.95 EndY=-3.15 EndZ=0
    g2: LineSegment StartX=41.65 StartY=-3.15 StartZ=0 EndX=41.65 EndY=-7.15 EndZ=0
    g3: LineSegment StartX=38.95 StartY=-7.15 StartZ=0 EndX=41.65 EndY=-7.15 EndZ=0
    g4: LineSegment StartX=38.95 StartY=-7.15 StartZ=0 EndX=36.25 EndY=-7.15 EndZ=0
    g5: LineSegment StartX=36.25 StartY=-3.15 StartZ=0 EndX=36.25 EndY=-7.15 EndZ=0
  constraints (16):
    c: Horizontal(g0)
    c: Distance(g0) = 2.7
    c: Horizontal(g1)
    c: Distance(g1) = 2.7
    c: Coincident(g1,g0)
    c: Block(g0)
    c: Coincident(g2,g0)
    c: Vertical(g2)
    c: Horizontal(g3)
    c: Coincident(g3,g2)
    c: Horizontal(g4)
    c: Coincident(g5,g1)
    c: Vertical(g5)
    c: Coincident(g5,g4)
    c: Block(g3)
    c: Block(g4)
FEATURE [Sketcher::SketchObject] Sketch022
  FullyConstrained = true
  Placement = pos=(0,-14.3,2.37) rot=(-1,0,0;2.03453rad)
  sketch-geometry (6):
    g0: LineSegment StartX=41.65 StartY=-3.15 StartZ=0 EndX=38.95 EndY=-3.15 EndZ=0
    g1: LineSegment StartX=36.25 StartY=-3.15 StartZ=0 EndX=38.95 EndY=-3.15 EndZ=0
    g2: LineSegment StartX=41.65 StartY=-3.15 StartZ=0 EndX=41.65 EndY=-7.15 EndZ=0
    g3: LineSegment StartX=38.95 StartY=-7.15 StartZ=0 EndX=41.65 EndY=-7.15 EndZ=0
    g4: LineSegment StartX=38.95 StartY=-7.15 StartZ=0 EndX=36.25 EndY=-7.15 EndZ=0
    g5: LineSegment StartX=36.25 StartY=-3.15 StartZ=0 EndX=36.25 EndY=-7.15 EndZ=0
  constraints (16):
    c: Horizontal(g0)
    c: Distance(g0) = 2.7
    c: Horizontal(g1)
    c: Distance(g1) = 2.7
    c: Coincident(g1,g0)
    c: Block(g0)
    c: Coincident(g2,g0)
    c: Vertical(g2)
    c: Horizontal(g3)
    c: Coincident(g3,g2)
    c: Horizontal(g4)
    c: Coincident(g5,g1)
    c: Vertical(g5)
    c: Coincident(g5,g4)
    c: Block(g3)
    c: Block(g4)
FEATURE [Sketcher::SketchObject] Sketch024
  FullyConstrained = true
  Placement = pos=(0,-14.3,2.37) rot=(-1,0,0;2.03453rad)
  sketch-geometry (4):
    g0: LineSegment StartX=49.5 StartY=-21.2 StartZ=0 EndX=49.5 EndY=-22.8 EndZ=0
    g1: LineSegment StartX=49.5 StartY=-22.8 StartZ=0 EndX=0.002238 EndY=-22.8 EndZ=0
    g2: LineSegment StartX=0.002238 StartY=-21.2 StartZ=0 EndX=0.002238 EndY=-22.8 EndZ=0
    g3: LineSegment StartX=49.5 StartY=-21.2 StartZ=0 EndX=0.002238 EndY=-21.2 EndZ=0
  constraints (10):
    c: Vertical(g0)
    c: Distance(g0) = 1.6
    c: Coincident(g1,g0)
    c: Horizontal(g1)
    c: Vertical(g2)
    c: Coincident(g2,g1)
    c: Coincident(g3,g0)
    c: Coincident(g3,g2)
    c: Horizontal(g3)
    c: Block(g3)
FEATURE [Sketcher::SketchObject] Sketch025
  FullyConstrained = true
  Placement = pos=(0,-14.3,2.37) rot=(-1,0,0;2.03453rad)
  sketch-geometry (4):
    g0: LineSegment StartX=0 StartY=1.5 StartZ=0 EndX=0 EndY=0 EndZ=0
    g1: LineSegment StartX=0 StartY=1.5 StartZ=0 EndX=5 EndY=1.5 EndZ=0
    g2: LineSegment StartX=5 StartY=1.5 StartZ=0 EndX=5 EndY=0 EndZ=0
    g3: LineSegment StartX=0 StartY=0 StartZ=0 EndX=5 EndY=0 EndZ=0
  constraints (13):
    c: Vertical(g0)
    c: Distance(g0) = 1.5
    c: Horizontal(g1)
    c: Distance(g1) = 5
    c: Coincident(g1,g0)
    c: Vertical(g2)
    c: Distance(g2) = 1.5
    c: Coincident(g2,g1)
    c: Block(g1)
    c: Block(g2)
    c: Block(g0)
    c: Coincident(g3,g0)
    c: Coincident(g3,g2)
FEATURE [Part::Extrusion] Extrude022  label="solenoidDriverBottomLipTopExtrude014"
  Base = -> Sketch025
  Dir = (0,0.894389,-0.447291)
  DirMode = 2
  FaceMakerClass = Part::FaceMakerBullseye
  LengthFwd = -6.5
  LengthRev = 0
  Placement = pos=(0,-15.45,20.3) rot=(1,0,0;1.5708rad)
  Solid = true
  Symmetric = false
FEATURE [Part::Fillet] Fillet013  label="solenoidDriverBottomLipTopFillet006"
  Base = -> Extrude022
  Edges = 1 edges r=1.4: [Edge6]
  Placement = pos=(5,0,0) rot=(0,0,1;0rad)
FEATURE [Sketcher::SketchObject] Sketch026
  FullyConstrained = true
  Placement = pos=(0,-14.3,2.37) rot=(-1,0,0;2.03453rad)
  sketch-geometry (4):
    g0: LineSegment StartX=0 StartY=1.5 StartZ=0 EndX=0 EndY=0 EndZ=0
    g1: LineSegment StartX=0 StartY=1.5 StartZ=0 EndX=5 EndY=1.5 EndZ=0
    g2: LineSegment StartX=5 StartY=1.5 StartZ=0 EndX=5 EndY=0 EndZ=0
    g3: LineSegment StartX=0 StartY=0 StartZ=0 EndX=5 EndY=0 EndZ=0
  constraints (13):
    c: Vertical(g0)
    c: Distance(g0) = 1.5
    c: Horizontal(g1)
    c: Distance(g1) = 5
    c: Coincident(g1,g0)
    c: Vertical(g2)
    c: Distance(g2) = 1.5
    c: Coincident(g2,g1)
    c: Block(g1)
    c: Block(g2)
    c: Block(g0)
    c: Coincident(g3,g0)
    c: Coincident(g3,g2)
FEATURE [Part::Extrusion] Extrude023  label="solenoidDriverBottomLipTopExtrude015"
  Base = -> Sketch026
  Dir = (0,0.894389,-0.447291)
  DirMode = 2
  FaceMakerClass = Part::FaceMakerBullseye
  LengthFwd = -6.5
  LengthRev = 0
  Placement = pos=(5,-14.15,19.65) rot=(1,0,0;1.5708rad)
  Solid = true
  Symmetric = false
FEATURE [Sketcher::SketchObject] Sketch027
  FullyConstrained = true
  Placement = pos=(0,-14.3,2.37) rot=(-1,0,0;2.03453rad)
  sketch-geometry (5):
    g0: LineSegment StartX=45.5 StartY=-21.2 StartZ=0 EndX=49.5 EndY=-21.2 EndZ=0
    g1: LineSegment StartX=49.5 StartY=0 StartZ=0 EndX=49.5 EndY=-21.2 EndZ=0
    g2: LineSegment StartX=49.5 StartY=0 StartZ=0 EndX=49.5 EndY=1.6 EndZ=0
    g3: LineSegment StartX=45.5 StartY=-21.2 StartZ=0 EndX=45.5 EndY=1.6 EndZ=0
    g4: LineSegment StartX=49.5 StartY=1.6 StartZ=0 EndX=45.5 EndY=1.6 EndZ=0
  constraints (14):
    c: Horizontal(g0)
    c: Distance(g0) = 4
    c: Coincident(g1,g0)
    c: Vertical(g1)
    c: Block(g1)
    c: Vertical(g2)
    c: Distance(g2) = 1.6
    c: Block(g2)
    c: Coincident(g3,g0)
    c: Vertical(g3)
    c: Coincident(g4,g2)
    c: Horizontal(g4)
    c: Block(g0)
    c: Coincident(g3,g4)
FEATURE [Part::Extrusion] Extrude024
  Base = -> Sketch027
  Dir = (0,0.894389,-0.447291)
  DirMode = 2
  FaceMakerClass = Part::FaceMakerBullseye
  LengthFwd = 6.34
  LengthRev = 0
  Placement = pos=(0,-5.59,1) rot=(0,0,1;0rad)
  Solid = true
  Symmetric = false
FEATURE [Part::Fillet] Fillet014  label="solenoidDriverSideBarFillet014"
  Base = -> Extrude024
  Edges = 1 edges r=1.4: [Edge14]
  Placement = pos=(0,0.9,-0.45) rot=(0,0,1;0rad)
FEATURE [Part::Revolution] Revolve  label="mainScrewStandRevolve"
  Angle = 360
  Axis = (0,0,1)
  Base = (0,0,0)
  FaceMakerClass = Part::FaceMakerBullseye
  Placement = pos=(121.35,-15.3,0) rot=(0,0,1;0rad)
  Solid = true
  Source = -> Sketch004
  Symmetric = false
FEATURE [Part::Extrusion] Extrude021  label="solenoidDriverTopLipLowerExtrude011"
  Base = -> Sketch024
  Dir = (0,0.894389,-0.447291)
  DirMode = 2
  FaceMakerClass = Part::FaceMakerBullseye
  LengthFwd = 5.05
  LengthRev = 0
  Solid = true
  Symmetric = false
FEATURE [Part::Fillet] Fillet012  label="solenoidDriverTopLipLowerFillet004"
  Base = -> Extrude021
  Edges = 1 edges r=1.2: [Edge7]
  Placement = pos=(0,-0.9,-1.35) rot=(0,0,1;0rad)
FEATURE [Part::Fillet] Fillet003  label="solenoidDriverTopLipLowerFillet003"
  Base = -> Extrude010
  Edges = 1 edges r=1.2: [Edge7]
  Placement = pos=(0,-3,-0.3) rot=(0,0,1;0rad)
FEATURE [Part::Extrusion] Extrude025  label="mainBodyUpperExtrude025"
  Base = -> Sketch001
  Dir = (0,0,1)
  DirMode = 2
  FaceMakerClass = Part::FaceMakerBullseye
  LengthFwd = 20
  LengthRev = 0
  Solid = true
  Symmetric = false
FEATURE [Part::MultiFuse] Fusion  label="solenoidDriverBottomLipFusion"
  Placement = pos=(0,-1.6,0) rot=(0,0,1;0rad)
  Shapes = -> [Fillet005,Fillet013,Extrude023,Extrude013]
FEATURE [Sketcher::SketchObject] Sketch028
  FullyConstrained = true
  Placement = pos=(0,-14.3,2.37) rot=(-1,0,0;2.03453rad)
  sketch-geometry (4):
    g0: LineSegment StartX=0 StartY=1.5 StartZ=0 EndX=0 EndY=0 EndZ=0
    g1: LineSegment StartX=0 StartY=1.5 StartZ=0 EndX=5 EndY=1.5 EndZ=0
    g2: LineSegment StartX=5 StartY=1.5 StartZ=0 EndX=5 EndY=0 EndZ=0
    g3: LineSegment StartX=0 StartY=0 StartZ=0 EndX=5 EndY=0 EndZ=0
  constraints (13):
    c: Vertical(g0)
    c: Distance(g0) = 1.5
    c: Horizontal(g1)
    c: Distance(g1) = 5
    c: Coincident(g1,g0)
    c: Vertical(g2)
    c: Distance(g2) = 1.5
    c: Coincident(g2,g1)
    c: Block(g1)
    c: Block(g2)
    c: Block(g0)
    c: Coincident(g3,g0)
    c: Coincident(g3,g2)
FEATURE [Part::Extrusion] Extrude026  label="solenoidDriverBottomLipTopExtrude016"
  Base = -> Sketch028
  Dir = (0,0.894389,-0.447291)
  DirMode = 2
  FaceMakerClass = Part::FaceMakerBullseye
  LengthFwd = -6.5
  LengthRev = 0
  Placement = pos=(5,-14.15,19.65) rot=(1,0,0;1.5708rad)
  Solid = true
  Symmetric = false
FEATURE [Sketcher::SketchObject] Sketch029
  FullyConstrained = true
  Placement = pos=(0,-14.3,2.37) rot=(-1,0,0;2.03453rad)
  sketch-geometry (4):
    g0: LineSegment StartX=0 StartY=1.5 StartZ=0 EndX=0 EndY=0 EndZ=0
    g1: LineSegment StartX=0 StartY=1.5 StartZ=0 EndX=5 EndY=1.5 EndZ=0
    g2: LineSegment StartX=5 StartY=1.5 StartZ=0 EndX=5 EndY=0 EndZ=0
    g3: LineSegment StartX=0 StartY=0 StartZ=0 EndX=5 EndY=0 EndZ=0
  constraints (13):
    c: Vertical(g0)
    c: Distance(g0) = 1.5
    c: Horizontal(g1)
    c: Distance(g1) = 5
    c: Coincident(g1,g0)
    c: Vertical(g2)
    c: Distance(g2) = 1.5
    c: Coincident(g2,g1)
    c: Block(g1)
    c: Block(g2)
    c: Block(g0)
    c: Coincident(g3,g0)
    c: Coincident(g3,g2)
FEATURE [Part::Extrusion] Extrude027  label="solenoidDriverBottomLipTopExtrude017"
  Base = -> Sketch029
  Dir = (0,0.894389,-0.447291)
  DirMode = 2
  FaceMakerClass = Part::FaceMakerBullseye
  LengthFwd = -6.5
  LengthRev = 0
  Placement = pos=(0,-14.15,19.65) rot=(1,0,0;1.5708rad)
  Solid = true
  Symmetric = false
FEATURE [Sketcher::SketchObject] Sketch030
  FullyConstrained = true
  Placement = pos=(0,-14.3,2.37) rot=(-1,0,0;2.03453rad)
  sketch-geometry (4):
    g0: LineSegment StartX=0 StartY=1.5 StartZ=0 EndX=0 EndY=0 EndZ=0
    g1: LineSegment StartX=0 StartY=1.5 StartZ=0 EndX=5 EndY=1.5 EndZ=0
    g2: LineSegment StartX=5 StartY=1.5 StartZ=0 EndX=5 EndY=0 EndZ=0
    g3: LineSegment StartX=0 StartY=0 StartZ=0 EndX=5 EndY=0 EndZ=0
  constraints (13):
    c: Vertical(g0)
    c: Distance(g0) = 1.5
    c: Horizontal(g1)
    c: Distance(g1) = 5
    c: Coincident(g1,g0)
    c: Vertical(g2)
    c: Distance(g2) = 1.5
    c: Coincident(g2,g1)
    c: Block(g1)
    c: Block(g2)
    c: Block(g0)
    c: Coincident(g3,g0)
    c: Coincident(g3,g2)
FEATURE [Sketcher::SketchObject] Sketch031
  FullyConstrained = true
  Placement = pos=(0,-14.3,2.37) rot=(-1,0,0;2.03453rad)
  sketch-geometry (6):
    g0: LineSegment StartX=45.5 StartY=-21.2 StartZ=0 EndX=49.5 EndY=-21.2 EndZ=0
    g1: LineSegment StartX=45.5 StartY=0 StartZ=0 EndX=49.5 EndY=0 EndZ=0
    g2: LineSegment StartX=49.5 StartY=0 StartZ=0 EndX=49.5 EndY=-21.2 EndZ=0
    g3: LineSegment StartX=4 StartY=0 StartZ=0 EndX=4 EndY=-21.2 EndZ=0
    g4: LineSegment StartX=45.5 StartY=-21.2 StartZ=0 EndX=4 EndY=-21.2 EndZ=0
    g5: LineSegment StartX=4 StartY=0 StartZ=0 EndX=45.5 EndY=0 EndZ=0
  constraints (16):
    c: Horizontal(g0)
    c: Distance(g0) = 4
    c: Horizontal(g1)
    c: Distance(g1) = 4
    c: Coincident(g2,g1)
    c: Coincident(g2,g0)
    c: Vertical(g2)
    c: Block(g2)
    c: Vertical(g3)
    c: Coincident(g4,g0)
    c: Horizontal(g4)
    c: Coincident(g4,g3)
    c: Coincident(g5,g1)
    c: Horizontal(g5)
    c: Block(g3)
    c: Block(g5)
FEATURE [Part::Extrusion] Extrude028  label="removeFromSolenoidDriverMainExtrude021"
  Base = -> Sketch031
  Dir = (0,0.894389,-0.447291)
  DirMode = 2
  FaceMakerClass = Part::FaceMakerBullseye
  LengthFwd = 3.1
  LengthRev = 0
  Placement = pos=(-4,-2.42,-0.8) rot=(0,0,1;0rad)
  Solid = true
  Symmetric = false
FEATURE [Part::Extrusion] Extrude029  label="solenoidDriverBottomLipTopExtrude018"
  Base = -> Sketch030
  Dir = (0,0.894389,-0.447291)
  DirMode = 2
  FaceMakerClass = Part::FaceMakerBullseye
  LengthFwd = -6.5
  LengthRev = 0
  Placement = pos=(5,-14.15,19.65) rot=(1,0,0;1.5708rad)
  Solid = true
  Symmetric = false
FEATURE [Sketcher::SketchObject] Sketch032
  FullyConstrained = true
  Placement = pos=(0,-14.3,2.37) rot=(-1,0,0;2.03453rad)
  sketch-geometry (4):
    g0: LineSegment StartX=0 StartY=1.5 StartZ=0 EndX=0 EndY=0 EndZ=0
    g1: LineSegment StartX=0 StartY=1.5 StartZ=0 EndX=5 EndY=1.5 EndZ=0
    g2: LineSegment StartX=5 StartY=1.5 StartZ=0 EndX=5 EndY=0 EndZ=0
    g3: LineSegment StartX=0 StartY=0 StartZ=0 EndX=5 EndY=0 EndZ=0
  constraints (13):
    c: Vertical(g0)
    c: Distance(g0) = 1.5
    c: Horizontal(g1)
    c: Distance(g1) = 5
    c: Coincident(g1,g0)
    c: Vertical(g2)
    c: Distance(g2) = 1.5
    c: Coincident(g2,g1)
    c: Block(g1)
    c: Block(g2)
    c: Block(g0)
    c: Coincident(g3,g0)
    c: Coincident(g3,g2)
FEATURE [Part::Extrusion] Extrude030  label="solenoidDriverBottomLipTopExtrude019"
  Base = -> Sketch032
  Dir = (0,0.894389,-0.447291)
  DirMode = 2
  FaceMakerClass = Part::FaceMakerBullseye
  LengthFwd = -6.5
  LengthRev = 0
  Placement = pos=(0,-14.15,19.65) rot=(1,0,0;1.5708rad)
  Solid = true
  Symmetric = false
FEATURE [Part::MultiFuse] Fusion004
  Placement = pos=(0,1.4,2.65) rot=(0,0,1;0rad)
  Shapes = -> [Extrude029,Extrude030]
FEATURE [Part::MultiFuse] Fusion003
  Placement = pos=(-2.3,0,0) rot=(0,0,1;0rad)
  Shapes = -> [Extrude028,Fusion004]
FEATURE [Sketcher::SketchObject] Sketch033
  FullyConstrained = true
  Placement = pos=(0,-14.3,2.37) rot=(-1,0,0;2.03453rad)
  sketch-geometry (4):
    g0: LineSegment StartX=0 StartY=1.5 StartZ=0 EndX=0 EndY=0 EndZ=0
    g1: LineSegment StartX=0 StartY=1.5 StartZ=0 EndX=5 EndY=1.5 EndZ=0
    g2: LineSegment StartX=5 StartY=1.5 StartZ=0 EndX=5 EndY=0 EndZ=0
    g3: LineSegment StartX=0 StartY=0 StartZ=0 EndX=5 EndY=0 EndZ=0
  constraints (13):
    c: Vertical(g0)
    c: Distance(g0) = 1.5
    c: Horizontal(g1)
    c: Distance(g1) = 5
    c: Coincident(g1,g0)
    c: Vertical(g2)
    c: Distance(g2) = 1.5
    c: Coincident(g2,g1)
    c: Block(g1)
    c: Block(g2)
    c: Block(g0)
    c: Coincident(g3,g0)
    c: Coincident(g3,g2)
FEATURE [Sketcher::SketchObject] Sketch034
  FullyConstrained = true
  Placement = pos=(0,-14.3,2.37) rot=(-1,0,0;2.03453rad)
  sketch-geometry (4):
    g0: LineSegment StartX=0 StartY=1.5 StartZ=0 EndX=4 EndY=1.5 EndZ=0
    g1: LineSegment StartX=4 StartY=1.5 StartZ=0 EndX=4 EndY=-2.5 EndZ=0
    g2: LineSegment StartX=4 StartY=-2.5 StartZ=0 EndX=0 EndY=-2.5 EndZ=0
    g3: LineSegment StartX=0 StartY=1.5 StartZ=0 EndX=0 EndY=-2.5 EndZ=0
  constraints (11):
    c: Horizontal(g0)
    c: Distance(g0) = 4
    c: Block(g0)
    c: Coincident(g1,g0)
    c: Vertical(g1)
    c: Distance(g1) = 4
    c: Coincident(g2,g1)
    c: Horizontal(g2)
    c: Distance(g2) = 4
    c: Coincident(g3,g0)
    c: Coincident(g3,g2)
FEATURE [Part::Extrusion] Extrude020  label="removeFromSolenoidDriverMainExtrude020"
  Base = -> Sketch020
  Dir = (0,0.894389,-0.447291)
  DirMode = 2
  FaceMakerClass = Part::FaceMakerBullseye
  LengthFwd = 3.1
  LengthRev = 0
  Placement = pos=(-4,-2.42,-0.8) rot=(0,0,1;0rad)
  Solid = true
  Symmetric = false
FEATURE [Part::Fillet] Fillet
  Base = -> Fusion003
  Edges = 1 edges r=10: [Edge5]
  Placement = pos=(-2,0,0) rot=(0,0,1;0rad)
FEATURE [Part::MultiFuse] Fusion001
  Placement = pos=(0,1.4,2.65) rot=(0,0,1;0rad)
  Shapes = -> [Extrude026,Extrude027]
FEATURE [Part::MultiFuse] Fusion002
  Shapes = -> [Extrude020,Fusion001]
FEATURE [Sketcher::SketchObject] Sketch035
  FullyConstrained = true
  Placement = pos=(0,-14.3,2.37) rot=(-1,0,0;2.03453rad)
  sketch-geometry (4):
    g0: LineSegment StartX=0 StartY=1.5 StartZ=0 EndX=0 EndY=0 EndZ=0
    g1: LineSegment StartX=0 StartY=1.5 StartZ=0 EndX=5 EndY=1.5 EndZ=0
    g2: LineSegment StartX=5 StartY=1.5 StartZ=0 EndX=5 EndY=0 EndZ=0
    g3: LineSegment StartX=0 StartY=0 StartZ=0 EndX=5 EndY=0 EndZ=0
  constraints (13):
    c: Vertical(g0)
    c: Distance(g0) = 1.5
    c: Horizontal(g1)
    c: Distance(g1) = 5
    c: Coincident(g1,g0)
    c: Vertical(g2)
    c: Distance(g2) = 1.5
    c: Coincident(g2,g1)
    c: Block(g1)
    c: Block(g2)
    c: Block(g0)
    c: Coincident(g3,g0)
    c: Coincident(g3,g2)
FEATURE [Sketcher::SketchObject] Sketch036
  FullyConstrained = true
  Placement = pos=(0,-14.3,2.37) rot=(-1,0,0;2.03453rad)
  sketch-geometry (4):
    g0: LineSegment StartX=0 StartY=1.5 StartZ=0 EndX=0 EndY=0 EndZ=0
    g1: LineSegment StartX=0 StartY=1.5 StartZ=0 EndX=5 EndY=1.5 EndZ=0
    g2: LineSegment StartX=5 StartY=1.5 StartZ=0 EndX=5 EndY=0 EndZ=0
    g3: LineSegment StartX=0 StartY=0 StartZ=0 EndX=5 EndY=0 EndZ=0
  constraints (13):
    c: Vertical(g0)
    c: Distance(g0) = 1.5
    c: Horizontal(g1)
    c: Distance(g1) = 5
    c: Coincident(g1,g0)
    c: Vertical(g2)
    c: Distance(g2) = 1.5
    c: Coincident(g2,g1)
    c: Block(g1)
    c: Block(g2)
    c: Block(g0)
    c: Coincident(g3,g0)
    c: Coincident(g3,g2)
FEATURE [Part::Extrusion] Extrude031  label="solenoidDriverBottomLipTopExtrude020"
  Base = -> Sketch035
  Dir = (0,0.894389,-0.447291)
  DirMode = 2
  FaceMakerClass = Part::FaceMakerBullseye
  LengthFwd = -6.5
  LengthRev = 0
  Placement = pos=(5,-14.15,19.65) rot=(1,0,0;1.5708rad)
  Solid = true
  Symmetric = false
FEATURE [Part::Extrusion] Extrude032  label="solenoidDriverBottomLipTopExtrude021"
  Base = -> Sketch036
  Dir = (0,0.894389,-0.447291)
  DirMode = 2
  FaceMakerClass = Part::FaceMakerBullseye
  LengthFwd = -6.5
  LengthRev = 0
  Placement = pos=(0,-14.15,19.65) rot=(1,0,0;1.5708rad)
  Solid = true
  Symmetric = false
FEATURE [Part::MultiFuse] Fusion009
  Placement = pos=(8,1.4,2.65) rot=(0,0,1;0rad)
  Shapes = -> [Extrude031,Extrude032]
FEATURE [Part::MultiFuse] Fusion010  label="removeFromSolenoidDriver"
  Shapes = -> [Fusion009,Fillet,Fusion002]
FEATURE [Sketcher::SketchObject] Sketch037
  FullyConstrained = true
  Placement = pos=(0,0,0) rot=(1,0,0;1.5708rad)
  sketch-geometry (4):
    g0: Circle CenterX=64.05 CenterY=16.5 CenterZ=0 NormalX=0 NormalY=0 NormalZ=1 AngleXU=0 Radius=2.7
    g1: Circle CenterX=64.05 CenterY=8.5 CenterZ=0 NormalX=0 NormalY=0 NormalZ=1 AngleXU=0 Radius=2.7
    g2: Circle CenterX=84.15 CenterY=8.5 CenterZ=0 NormalX=0 NormalY=0 NormalZ=1 AngleXU=0 Radius=2.7
    g3: Circle CenterX=84.15 CenterY=16.5 CenterZ=0 NormalX=0 NormalY=0 NormalZ=1 AngleXU=0 Radius=2.7
  constraints (4):
    c: Block(g2)
    c: Block(g3)
    c: Block(g0)
    c: Block(g1)
FEATURE [Part::Extrusion] Extrude033  label="removeFromMainBodyToCreateScrewHoleCounterSinks001"
  Base = -> Sketch037
  Dir = (0,-1,1.1e-15)
  DirMode = 2
  FaceMakerClass = Part::FaceMakerBullseye
  LengthFwd = 1.9
  LengthRev = 0
  Placement = pos=(0.8,0,0) rot=(0,0,1;0rad)
  Solid = true
  Symmetric = false
FEATURE [Part::MultiFuse] Fusion011  label="removeFromMainBodyToCreateScrewHoleCounterSinks001Fusion011"
  Shapes = -> [Extrude014,Extrude033]
FEATURE [Sketcher::SketchObject] Sketch038
  FullyConstrained = true
  Placement = pos=(0,-14.3,2.37) rot=(-1,0,0;2.03453rad)
  sketch-geometry (4):
    g0: LineSegment StartX=33.9 StartY=-9.7 StartZ=0 EndX=33.9 EndY=-1.5 EndZ=0
    g1: LineSegment StartX=33.9 StartY=-1.5 StartZ=0 EndX=44.5 EndY=-1.5 EndZ=0
    g2: LineSegment StartX=33.9 StartY=-9.7 StartZ=0 EndX=44.5 EndY=-9.7 EndZ=0
    g3: LineSegment StartX=44.5 StartY=-1.5 StartZ=0 EndX=44.5 EndY=-9.7 EndZ=0
  constraints (10):
    c: Vertical(g0)
    c: Coincident(g1,g0)
    c: Horizontal(g1)
    c: Block(g1)
    c: Block(g0)
    c: Coincident(g2,g0)
    c: Horizontal(g2)
    c: Coincident(g3,g1)
    c: Coincident(g3,g2)
    c: Vertical(g3)
FEATURE [Part::Extrusion] Extrude034
  Base = -> Sketch038
  Dir = (0,0.894389,-0.447291)
  DirMode = 2
  FaceMakerClass = Part::FaceMakerBullseye
  LengthFwd = 16
  LengthRev = 0
  Placement = pos=(0,-22,7) rot=(0,0,1;0rad)
  Solid = true
  Symmetric = false
FEATURE [Sketcher::SketchObject] Sketch039
  FullyConstrained = true
  Placement = pos=(0,-14.3,2.37) rot=(-1,0,0;2.03453rad)
  sketch-geometry (4):
    g0: LineSegment StartX=5.5 StartY=-7.7 StartZ=0 EndX=13.3 EndY=-7.7 EndZ=0
    g1: LineSegment StartX=13.3 StartY=-7.7 StartZ=0 EndX=13.3 EndY=-13.1 EndZ=0
    g2: LineSegment StartX=13.3 StartY=-13.1 StartZ=0 EndX=5.5 EndY=-13.1 EndZ=0
    g3: LineSegment StartX=5.5 StartY=-7.7 StartZ=0 EndX=5.5 EndY=-13.1 EndZ=0
  constraints (12):
    c: Horizontal(g0)
    c: Distance(g0) = 7.8
    c: Coincident(g1,g0)
    c: Vertical(g1)
    c: Distance(g1) = 5.4
    c: Coincident(g2,g1)
    c: Horizontal(g2)
    c: Vertical(g3)
    c: Coincident(g3,g2)
    c: Block(g0)
    c: Block(g2)
    c: Block(g3)
FEATURE [Part::Extrusion] Extrude035  label="removeToMakeHoleForConnectorExtrude035"
  Base = -> Sketch039
  Dir = (0,0.894389,-0.447291)
  DirMode = 2
  FaceMakerClass = Part::FaceMakerBullseye
  LengthFwd = 15
  LengthRev = 0
  Placement = pos=(-4,-22,9.6469) rot=(0,0,1;0rad)
  Solid = true
  Symmetric = false
FEATURE [App::MeasureDistance] Distance  label="Distance: 4.00 mm"
  Distance = 4.00184
  P1 = (119.349,-15.3,8)
  P2 = (123.351,-15.3,8)
FEATURE [App::MeasureDistance] Distance001  label="Distance: 3.80 mm"
  Distance = 3.8
  P1 = (119.45,-15.3,8)
  P2 = (123.25,-15.3,8)
FEATURE [Part::Fillet] Fillet015
  Base = -> Extrude009
  Edges = 1 edges r=1.59: [Edge7]
FEATURE [Part::Fillet] Fillet016
  Base = -> Extrude017
  Edges = 1 edges r=1.49: [Edge12]
FEATURE [Part::Fillet] Fillet017
  Base = -> Fillet016
  Edges = 1 edges r=1.45: [Edge8]
FEATURE [Part::MultiFuse] Fusion012  label="main"
  Shapes = -> [Extrude,Revolve,Extrude005,Fillet003,Fillet012,Fillet014,Extrude025,Fusion,Fillet015,Fillet017]
FEATURE [Part::Cut] Cut001
  Base = -> Fusion012
  Tool = -> Box003
FEATURE [Part::Cut] Cut002
  Base = -> Cut001
  Tool = -> Box002
FEATURE [Part::Cut] Cut003
  Base = -> Cut002
  Tool = -> Cut
FEATURE [Part::Cut] Cut004
  Base = -> Cut003
  Tool = -> Extrude019
FEATURE [Part::Cut] Cut005
  Base = -> Cut004
  Tool = -> Fusion011
FEATURE [Part::Cut] Cut006
  Base = -> Cut005
  Tool = -> Extrude004
FEATURE [Part::Cut] Cut007
  Base = -> Cut006
  Tool = -> Extrude015
FEATURE [Part::Cut] Cut008
  Base = -> Cut007
  Tool = -> Extrude008
FEATURE [Part::Cut] Cut009
  Base = -> Cut008
  Tool = -> Fusion010
FEATURE [App::MeasureDistance] Distance002  label="Distance: 2.05 mm"
  Distance = 2.05453
  P1 = (1.5,-23.0732,21.402)
  P2 = (6e-15,-23,20)
FEATURE [Part::Cut] Cut010
  Base = -> Cut009
  Tool = -> Extrude035
FEATURE [Part::Cut] Cut011
  Base = -> Cut010
  Tool = -> Extrude034
FEATURE [Part::Box] Box004  label="Cube004"
  AttacherType = Attacher::AttachEngine3D
  Height = 10
  Length = 200
  Placement = pos=(-30,0,0) rot=(0,0,1;0rad)
  Width = 10
FEATURE [Part::Fillet] Fillet020
  Base = -> Box004
  Edges = 1 edges r=3.6: [Edge12]
FEATURE [Part::Box] Box005  label="Cube005"
  AttacherType = Attacher::AttachEngine3D
  Height = 10
  Length = 198
  Placement = pos=(-30,0,0) rot=(0,0,1;0rad)
  Width = 10
FEATURE [Part::Cut] Cut012
  Base = -> Box005
  Tool = -> Fillet020
FEATURE [Part::Box] Box006  label="Cube006"
  AttacherType = Attacher::AttachEngine3D
  Height = 5
  Length = 200
  Placement = pos=(-30,6.4,10) rot=(1,0,0;0rad)
  Width = 5
FEATURE [Part::Box] Box007  label="Cube007"
  AttacherType = Attacher::AttachEngine3D
  Height = 5
  Length = 200
  Placement = pos=(-30,6.4,10) rot=(1,0,0;0.872665rad)
  Width = 5
FEATURE [Part::MultiFuse] Fusion013  label="removeFromMainFusion013"
  Placement = pos=(0,-10,10) rot=(0,0,1;0rad)
  Shapes = -> [Box007,Box006,Cut012]
FEATURE [Mesh::Feature] v0_98_Cut013  label="v0_98-Cut013"
FEATURE [App::MeasureDistance] Distance003  label="Distance: 7.18 mm"
  Distance = 7.17719
  P1 = (117.773,-15.3145,-2.4)
  P2 = (124.951,-15.2973,-2.4)
FEATURE [Sketcher::SketchObject] Sketch040
  FullyConstrained = true
  Placement = pos=(0,-14.3,2.37) rot=(-1,0,0;2.03453rad)
  sketch-geometry (4):
    g0: LineSegment StartX=0 StartY=1.5 StartZ=0 EndX=0 EndY=0 EndZ=0
    g1: LineSegment StartX=0 StartY=1.5 StartZ=0 EndX=5 EndY=1.5 EndZ=0
    g2: LineSegment StartX=5 StartY=1.5 StartZ=0 EndX=5 EndY=0 EndZ=0
    g3: LineSegment StartX=0 StartY=0 StartZ=0 EndX=5 EndY=0 EndZ=0
  constraints (13):
    c: Vertical(g0)
    c: Distance(g0) = 1.5
    c: Horizontal(g1)
    c: Distance(g1) = 5
    c: Coincident(g1,g0)
    c: Vertical(g2)
    c: Distance(g2) = 1.5
    c: Coincident(g2,g1)
    c: Block(g1)
    c: Block(g2)
    c: Block(g0)
    c: Coincident(g3,g0)
    c: Coincident(g3,g2)
FEATURE [Part::Extrusion] Extrude036
  Base = -> Sketch040
  Dir = (0,0.894389,-0.447291)
  DirMode = 2
  FaceMakerClass = Part::FaceMakerBullseye
  LengthFwd = 1.4
  LengthRev = 0
  Placement = pos=(0,8.25,17.58) rot=(0,0,1;0rad)
  Solid = true
  Symmetric = false
FEATURE [Sketcher::SketchObject] Sketch041
  FullyConstrained = true
  Placement = pos=(0,-14.3,2.37) rot=(-1,0,0;2.03453rad)
  sketch-geometry (4):
    g0: LineSegment StartX=0 StartY=1.5 StartZ=0 EndX=0 EndY=0 EndZ=0
    g1: LineSegment StartX=0 StartY=1.5 StartZ=0 EndX=5 EndY=1.5 EndZ=0
    g2: LineSegment StartX=5 StartY=1.5 StartZ=0 EndX=5 EndY=0 EndZ=0
    g3: LineSegment StartX=0 StartY=0 StartZ=0 EndX=5 EndY=0 EndZ=0
  constraints (13):
    c: Vertical(g0)
    c: Distance(g0) = 1.5
    c: Horizontal(g1)
    c: Distance(g1) = 5
    c: Coincident(g1,g0)
    c: Vertical(g2)
    c: Distance(g2) = 1.5
    c: Coincident(g2,g1)
    c: Block(g1)
    c: Block(g2)
    c: Block(g0)
    c: Coincident(g3,g0)
    c: Coincident(g3,g2)
FEATURE [Part::Extrusion] Extrude037
  Base = -> Sketch041
  Dir = (0,0.894389,-0.447291)
  DirMode = 2
  FaceMakerClass = Part::FaceMakerBullseye
  LengthFwd = 1.4
  LengthRev = 0
  Placement = pos=(0,6.11,13.33) rot=(0,0,1;0rad)
  Solid = true
  Symmetric = false
FEATURE [Part::MultiFuse] Fusion014  label="screwSpacerFusion014"
  Shapes = -> [Extrude037,Extrude036]
FEATURE [Sketcher::SketchObject] Sketch042
  FullyConstrained = true
  Placement = pos=(0,-14.3,2.37) rot=(-1,0,0;2.03453rad)
  sketch-geometry (4):
    g0: LineSegment StartX=0 StartY=1.5 StartZ=0 EndX=0 EndY=0 EndZ=0
    g1: LineSegment StartX=0 StartY=1.5 StartZ=0 EndX=5 EndY=1.5 EndZ=0
    g2: LineSegment StartX=5 StartY=1.5 StartZ=0 EndX=5 EndY=0 EndZ=0
    g3: LineSegment StartX=0 StartY=0 StartZ=0 EndX=5 EndY=0 EndZ=0
  constraints (13):
    c: Vertical(g0)
    c: Distance(g0) = 1.5
    c: Horizontal(g1)
    c: Distance(g1) = 5
    c: Coincident(g1,g0)
    c: Vertical(g2)
    c: Distance(g2) = 1.5
    c: Coincident(g2,g1)
    c: Block(g1)
    c: Block(g2)
    c: Block(g0)
    c: Coincident(g3,g0)
    c: Coincident(g3,g2)
FEATURE [Part::Extrusion] Extrude038
  Base = -> Sketch042
  Dir = (0,0.894389,-0.447291)
  DirMode = 2
  FaceMakerClass = Part::FaceMakerBullseye
  LengthFwd = 1.4
  LengthRev = 0
  Placement = pos=(0,8.459,18) rot=(0,0,1;0rad)
  Solid = true
  Symmetric = false
FEATURE [Part::MultiFuse] Fusion015  label="screwSpacerFusion014Fusion015"
  Placement = pos=(0,0.35,-0.18) rot=(0,0,1;0rad)
  Shapes = -> [Extrude038,Fusion014]
FEATURE [Part::Cylinder] Cylinder
  Angle = 360
  AttacherType = Attacher::AttachEngine3D
  Height = 10
  Placement = pos=(0,10,0) rot=(0,0,1;0rad)
  Radius = 1.5
FEATURE [Part::Cylinder] Cylinder001
  Angle = 360
  AttacherType = Attacher::AttachEngine3D
  Height = 10
  Placement = pos=(3,10,0) rot=(0,0,1;0rad)
  Radius = 1.5
FEATURE [Part::Box] Box008  label="Cube008"
  AttacherType = Attacher::AttachEngine3D
  Height = 10
  Length = 3
  Placement = pos=(0,8.5,0) rot=(0,0,1;0rad)
  Width = 3
FEATURE [Part::MultiFuse] Fusion016  label="holeForWireFusion016"
  Shapes = -> [Cylinder001,Box008,Cylinder]
FEATURE [Part::Box] Box009  label="Cube009"
  AttacherType = Attacher::AttachEngine3D
  Height = 10
  Length = 3
  Placement = pos=(0,8.5,0) rot=(0,0,1;0rad)
  Width = 3
FEATURE [Part::Cylinder] Cylinder002
  Angle = 360
  AttacherType = Attacher::AttachEngine3D
  Height = 10
  Placement = pos=(0,10,0) rot=(0,0,1;0rad)
  Radius = 1.5
FEATURE [Part::Cylinder] Cylinder003
  Angle = 360
  AttacherType = Attacher::AttachEngine3D
  Height = 10
  Placement = pos=(3,10,0) rot=(0,0,1;0rad)
  Radius = 1.5
FEATURE [Part::MultiFuse] Fusion017  label="holeForWireFusion017"
  Placement = pos=(0,0,10) rot=(0,0,1;0rad)
  Shapes = -> [Cylinder003,Box009,Cylinder002]
FEATURE [Part::MultiFuse] Fusion018  label="holeForWireFusion018"
  Placement = pos=(0,0,0) rot=(0,1,0;-1.5708rad)
  Shapes = -> [Fusion017,Fusion016]
FEATURE [Part::Box] Box010  label="Cube010"
  AttacherType = Attacher::AttachEngine3D
  Height = 0.1
  Length = 0.1
  Placement = pos=(-2,10,0) rot=(0,0.995037,0.099504;0rad)
  Width = 0.1
FEATURE [Part::MultiFuse] Fusion019
  Placement = pos=(0,10,0) rot=(1,0,0;1.5708rad)
  Shapes = -> [Box010,Fusion018]
FEATURE [Part::Box] Box011  label="Cube011"
  AttacherType = Attacher::AttachEngine3D
  Height = 0.1
  Length = 1.1
  Placement = pos=(-2,10,10) rot=(0,0.995037,0.099504;0rad)
  Width = 0.1
FEATURE [Part::MultiFuse] Fusion020
  Placement = pos=(0,0,0) rot=(0,1,0;0.349066rad)
  Shapes = -> [Box011,Fusion019]
FEATURE [Part::Box] Box012  label="Cube012"
  AttacherType = Attacher::AttachEngine3D
  Height = 0.1
  Length = 1.1
  Placement = pos=(-2,10,10) rot=(0,0.995037,0.099504;0rad)
  Width = 0.1
FEATURE [Part::MultiFuse] Fusion021
  Placement = pos=(0,30,0) rot=(0,0,1;-2.6529rad)
  Shapes = -> [Box012,Fusion020]
FEATURE [Part::Box] Box013  label="Cube013"
  AttacherType = Attacher::AttachEngine3D
  Height = 0.1
  Length = 1.1
  Placement = pos=(2,19,10) rot=(0,0.995037,0.099504;0rad)
  Width = 0.1
FEATURE [Part::MultiFuse] Fusion022  label="holeForWire"
  Placement = pos=(15,-49.8,-8.2) rot=(0,0,1;0rad)
  Shapes = -> [Box013,Fusion021]
FEATURE [Part::Cut] Cut013
  Base = -> Cut011
  Tool = -> Fusion013
FEATURE [Part::Cut] Cut014
  Base = -> Cut013
  Tool = -> Fusion022
FEATURE [Sketcher::SketchObject] Sketch043
  FullyConstrained = true
  MapMode = 4
  Placement = pos=(0,0,0) rot=(0.57735,0.57735,0.57735;2.0944rad)
  Support = -> [Cut014]
  sketch-geometry (14):
    g0: LineSegment StartX=6.08745 StartY=-4.11588 StartZ=0 EndX=6.08745 EndY=-2.11589 EndZ=0
    g1: LineSegment StartX=3.58745 StartY=2.38411 StartZ=0 EndX=3.58745 EndY=4.38411 EndZ=0
    g2: LineSegment StartX=8.08745 StartY=1.38411 StartZ=0 EndX=8.08745 EndY=-1.11589 EndZ=0
    g3: ArcOfCircle CenterX=7.08745 CenterY=-1.11589 CenterZ=0 NormalX=0 NormalY=0 NormalZ=1 AngleXU=0 Radius=1 StartAngle=4.71239 EndAngle=6.28319
    g4: LineSegment StartX=6.08745 StartY=-2.11589 StartZ=0 EndX=7.08745 EndY=-2.11589 EndZ=0
    g5: LineSegment StartX=6.08745 StartY=-4.11588 StartZ=0 EndX=7.08745 EndY=-4.11588 EndZ=0
    g6: ArcOfCircle CenterX=7.08745 CenterY=-1.11589 CenterZ=0 NormalX=0 NormalY=0 NormalZ=1 AngleXU=0 Radius=3 StartAngle=4.71239 EndAngle=6.28319
    g7: ArcOfCircle CenterX=7.08745 CenterY=1.38411 CenterZ=0 NormalX=0 NormalY=0 NormalZ=1 AngleXU=0 Radius=1 StartAngle=5.35e-14 EndAngle=1.5708
    g8: LineSegment StartX=3.58745 StartY=4.38411 StartZ=0 EndX=7.08745 EndY=4.38411 EndZ=0
    g9: LineSegment StartX=10.0875 StartY=-1.11588 StartZ=0 EndX=10.0875 EndY=1.38411 EndZ=0
    g10: ArcOfCircle CenterX=7.08745 CenterY=1.38411 CenterZ=0 NormalX=0 NormalY=0 NormalZ=1 AngleXU=0 Radius=3 StartAngle=3.57e-14 EndAngle=1.5708
    g11: LineSegment StartX=3.58745 StartY=2.38411 StartZ=0 EndX=3.58745 EndY=1.38411 EndZ=0
    g12: ArcOfCircle CenterX=4.58745 CenterY=1.38412 CenterZ=0 NormalX=0 NormalY=0 NormalZ=1 AngleXU=0 Radius=1 StartAngle=1.57081 EndAngle=3.14159
    g13: LineSegment StartX=4.58744 StartY=2.38411 StartZ=0 EndX=7.08745 EndY=2.38411 EndZ=0
  constraints (33):
    c: Vertical(g0)
    c: Vertical(g1)
    c: Distance(g1) = 2
    c: Block(g0)
    c: Block(g2)
    c: Coincident(g3,g2)
    c: Coincident(g4,g0)
    c: Coincident(g4,g3)
    c: Horizontal(g4)
    c: Block(g3)
    c: Coincident(g5,g0)
    c: Horizontal(g5)
    c: Coincident(g6,g3)
    c: Block(g6)
    c: Block(g5)
    c: Coincident(g7,g2)
    c: Block(g7)
    c: Coincident(g8,g1)
    c: Coincident(g9,g6)
    c: Vertical(g9)
    c: Coincident(g10,g7)
    c: Block(g10)
    c: Block(g8)
    c: Block(g9)
    c: Coincident(g11,g1)
    c: Vertical(g11)
    c: Distance(g11) = 1
    c: Coincident(g12,g11)
    c: Coincident(g13,g12)
    c: Coincident(g13,g7)
    c: Horizontal(g13)
    c: Block(g13)
    c: Block(g12)
FEATURE [Sketcher::SketchObject] Sketch044
  FullyConstrained = true
  MapMode = 4
  Placement = pos=(0,0,0) rot=(0.57735,0.57735,0.57735;2.0944rad)
  Support = -> [Cut014]
  sketch-geometry (14):
    g0: LineSegment StartX=6.08745 StartY=-4.11588 StartZ=0 EndX=6.08745 EndY=-2.11589 EndZ=0
    g1: LineSegment StartX=8.08745 StartY=1.38411 StartZ=0 EndX=8.08745 EndY=-1.11589 EndZ=0
    g2: ArcOfCircle CenterX=7.08745 CenterY=-1.11589 CenterZ=0 NormalX=0 NormalY=0 NormalZ=1 AngleXU=0 Radius=1 StartAngle=4.71239 EndAngle=6.28319
    g3: LineSegment StartX=6.08745 StartY=-2.11589 StartZ=0 EndX=7.08745 EndY=-2.11589 EndZ=0
    g4: LineSegment StartX=6.08745 StartY=-4.11588 StartZ=0 EndX=7.08745 EndY=-4.11588 EndZ=0
    g5: ArcOfCircle CenterX=7.08745 CenterY=-1.11589 CenterZ=0 NormalX=0 NormalY=0 NormalZ=1 AngleXU=0 Radius=3 StartAngle=4.71239 EndAngle=6.28319
    g6: ArcOfCircle CenterX=7.08745 CenterY=1.38411 CenterZ=0 NormalX=0 NormalY=0 NormalZ=1 AngleXU=0 Radius=1 StartAngle=5.35e-14 EndAngle=1.5708
    g7: LineSegment StartX=10.0875 StartY=-1.11588 StartZ=0 EndX=10.0875 EndY=1.38411 EndZ=0
    g8: ArcOfCircle CenterX=7.08745 CenterY=1.38411 CenterZ=0 NormalX=0 NormalY=0 NormalZ=1 AngleXU=0 Radius=3 StartAngle=3.57e-14 EndAngle=1.5708
    g9: ArcOfCircle CenterX=4.58745 CenterY=1.38412 CenterZ=0 NormalX=0 NormalY=0 NormalZ=1 AngleXU=0 Radius=1 StartAngle=1.57081 EndAngle=3.14159
    g10: LineSegment StartX=4.58744 StartY=2.38411 StartZ=0 EndX=7.08745 EndY=2.38411 EndZ=0
    g11: LineSegment StartX=4.58745 StartY=4.38411 StartZ=0 EndX=7.08745 EndY=4.38411 EndZ=0
    g12: ArcOfCircle CenterX=4.58745 CenterY=5.38411 CenterZ=0 NormalX=0 NormalY=0 NormalZ=1 AngleXU=0 Radius=1 StartAngle=3.14159 EndAngle=4.71239
    g13: LineSegment StartX=3.58745 StartY=5.38411 StartZ=0 EndX=3.58745 EndY=1.38411 EndZ=0
  constraints (33):
    c: Vertical(g0)
    c: Block(g0)
    c: Block(g1)
    c: Coincident(g2,g1)
    c: Coincident(g3,g0)
    c: Coincident(g3,g2)
    c: Horizontal(g3)
    c: Block(g2)
    c: Coincident(g4,g0)
    c: Horizontal(g4)
    c: Coincident(g5,g2)
    c: Block(g5)
    c: Block(g4)
    c: Coincident(g6,g1)
    c: Block(g6)
    c: Coincident(g7,g5)
    c: Vertical(g7)
    c: Coincident(g8,g6)
    c: Block(g8)
    c: Block(g7)
    c: Coincident(g10,g9)
    c: Coincident(g10,g6)
    c: Horizontal(g10)
    c: Block(g10)
    c: Block(g9)
    c: Coincident(g11,g8)
    c: Horizontal(g11)
    c: Block(g12)
    c: Block(g11)
    c: Coincident(g13,g12)
    c: Coincident(g13,g9)
    c: Vertical(g13)
    c: Tangent(g13,g9)
FEATURE [Part::Extrusion] Extrude039
  Base = -> Sketch044
  Dir = (1,0,0)
  DirMode = 2
  FaceMakerClass = Part::FaceMakerBullseye
  LengthFwd = 10
  LengthRev = 0
  Placement = pos=(8,-22.615,4.115) rot=(0,0,1;3.14159rad)
  Solid = true
  Symmetric = false
FEATURE [App::MeasureDistance] Distance004  label="Distance: 42.16 mm"
  Distance = 42.1607
  P1 = (14.6786,-26.2,1.24491)
  P2 = (-27.4815,-26.2,1.03853)
FEATURE [Sketcher::SketchObject] Sketch045
  FullyConstrained = true
  MapMode = 4
  Placement = pos=(0,0,0) rot=(0.57735,0.57735,0.57735;2.0944rad)
  Support = -> [Cut014]
  sketch-geometry (14):
    g0: LineSegment StartX=6.08745 StartY=-4.11588 StartZ=0 EndX=6.08745 EndY=-2.11589 EndZ=0
    g1: LineSegment StartX=8.08745 StartY=1.38411 StartZ=0 EndX=8.08745 EndY=-1.11589 EndZ=0
    g2: ArcOfCircle CenterX=7.08745 CenterY=-1.11589 CenterZ=0 NormalX=0 NormalY=0 NormalZ=1 AngleXU=0 Radius=1 StartAngle=4.71239 EndAngle=6.28319
    g3: LineSegment StartX=6.08745 StartY=-2.11589 StartZ=0 EndX=7.08745 EndY=-2.11589 EndZ=0
    g4: LineSegment StartX=6.08745 StartY=-4.11588 StartZ=0 EndX=7.08745 EndY=-4.11588 EndZ=0
    g5: ArcOfCircle CenterX=7.08745 CenterY=-1.11589 CenterZ=0 NormalX=0 NormalY=0 NormalZ=1 AngleXU=0 Radius=3 StartAngle=4.71239 EndAngle=6.28319
    g6: ArcOfCircle CenterX=7.08745 CenterY=1.38411 CenterZ=0 NormalX=0 NormalY=0 NormalZ=1 AngleXU=0 Radius=1 StartAngle=5.35e-14 EndAngle=1.5708
    g7: LineSegment StartX=10.0875 StartY=-1.11588 StartZ=0 EndX=10.0875 EndY=1.38411 EndZ=0
    g8: ArcOfCircle CenterX=7.08745 CenterY=1.38411 CenterZ=0 NormalX=0 NormalY=0 NormalZ=1 AngleXU=0 Radius=3 StartAngle=3.57e-14 EndAngle=1.5708
    g9: ArcOfCircle CenterX=4.58745 CenterY=1.38412 CenterZ=0 NormalX=0 NormalY=0 NormalZ=1 AngleXU=0 Radius=1 StartAngle=1.57081 EndAngle=3.14159
    g10: LineSegment StartX=4.58744 StartY=2.38411 StartZ=0 EndX=7.08745 EndY=2.38411 EndZ=0
    g11: LineSegment StartX=4.58745 StartY=4.38411 StartZ=0 EndX=7.08745 EndY=4.38411 EndZ=0
    g12: ArcOfCircle CenterX=4.58745 CenterY=5.38411 CenterZ=0 NormalX=0 NormalY=0 NormalZ=1 AngleXU=0 Radius=1 StartAngle=3.14159 EndAngle=4.71239
    g13: LineSegment StartX=3.58745 StartY=5.38411 StartZ=0 EndX=3.58745 EndY=1.38411 EndZ=0
  constraints (33):
    c: Vertical(g0)
    c: Block(g0)
    c: Block(g1)
    c: Coincident(g2,g1)
    c: Coincident(g3,g0)
    c: Coincident(g3,g2)
    c: Horizontal(g3)
    c: Block(g2)
    c: Coincident(g4,g0)
    c: Horizontal(g4)
    c: Coincident(g5,g2)
    c: Block(g5)
    c: Block(g4)
    c: Coincident(g6,g1)
    c: Block(g6)
    c: Coincident(g7,g5)
    c: Vertical(g7)
    c: Coincident(g8,g6)
    c: Block(g8)
    c: Block(g7)
    c: Coincident(g10,g9)
    c: Coincident(g10,g6)
    c: Horizontal(g10)
    c: Block(g10)
    c: Block(g9)
    c: Coincident(g11,g8)
    c: Horizontal(g11)
    c: Block(g12)
    c: Block(g11)
    c: Coincident(g13,g12)
    c: Coincident(g13,g9)
    c: Vertical(g13)
    c: Tangent(g13,g9)
FEATURE [Part::Extrusion] Extrude040
  Base = -> Sketch045
  Dir = (1,0,0)
  DirMode = 2
  FaceMakerClass = Part::FaceMakerBullseye
  LengthFwd = 10
  LengthRev = 0
  Placement = pos=(-17.5,-22.615,4.115) rot=(0,0,1;3.14159rad)
  Solid = true
  Symmetric = false
FEATURE [Sketcher::SketchObject] Sketch046
  FullyConstrained = true
  MapMode = 4
  Placement = pos=(0,0,0) rot=(0.57735,0.57735,0.57735;2.0944rad)
  Support = -> [Cut014]
  sketch-geometry (14):
    g0: LineSegment StartX=6.08745 StartY=-4.11588 StartZ=0 EndX=6.08745 EndY=-2.11589 EndZ=0
    g1: LineSegment StartX=8.08745 StartY=1.38411 StartZ=0 EndX=8.08745 EndY=-1.11589 EndZ=0
    g2: ArcOfCircle CenterX=7.08745 CenterY=-1.11589 CenterZ=0 NormalX=0 NormalY=0 NormalZ=1 AngleXU=0 Radius=1 StartAngle=4.71239 EndAngle=6.28319
    g3: LineSegment StartX=6.08745 StartY=-2.11589 StartZ=0 EndX=7.08745 EndY=-2.11589 EndZ=0
    g4: LineSegment StartX=6.08745 StartY=-4.11588 StartZ=0 EndX=7.08745 EndY=-4.11588 EndZ=0
    g5: ArcOfCircle CenterX=7.08745 CenterY=-1.11589 CenterZ=0 NormalX=0 NormalY=0 NormalZ=1 AngleXU=0 Radius=3 StartAngle=4.71239 EndAngle=6.28319
    g6: ArcOfCircle CenterX=7.08745 CenterY=1.38411 CenterZ=0 NormalX=0 NormalY=0 NormalZ=1 AngleXU=0 Radius=1 StartAngle=5.35e-14 EndAngle=1.5708
    g7: LineSegment StartX=10.0875 StartY=-1.11588 StartZ=0 EndX=10.0875 EndY=1.38411 EndZ=0
    g8: ArcOfCircle CenterX=7.08745 CenterY=1.38411 CenterZ=0 NormalX=0 NormalY=0 NormalZ=1 AngleXU=0 Radius=3 StartAngle=3.57e-14 EndAngle=1.5708
    g9: ArcOfCircle CenterX=4.58745 CenterY=1.38412 CenterZ=0 NormalX=0 NormalY=0 NormalZ=1 AngleXU=0 Radius=1 StartAngle=1.57081 EndAngle=3.14159
    g10: LineSegment StartX=4.58744 StartY=2.38411 StartZ=0 EndX=7.08745 EndY=2.38411 EndZ=0
    g11: LineSegment StartX=4.58745 StartY=4.38411 StartZ=0 EndX=7.08745 EndY=4.38411 EndZ=0
    g12: ArcOfCircle CenterX=4.58745 CenterY=5.38411 CenterZ=0 NormalX=0 NormalY=0 NormalZ=1 AngleXU=0 Radius=1 StartAngle=3.14159 EndAngle=4.71239
    g13: LineSegment StartX=3.58745 StartY=5.38411 StartZ=0 EndX=3.58745 EndY=1.38411 EndZ=0
  constraints (33):
    c: Vertical(g0)
    c: Block(g0)
    c: Block(g1)
    c: Coincident(g2,g1)
    c: Coincident(g3,g0)
    c: Coincident(g3,g2)
    c: Horizontal(g3)
    c: Block(g2)
    c: Coincident(g4,g0)
    c: Horizontal(g4)
    c: Coincident(g5,g2)
    c: Block(g5)
    c: Block(g4)
    c: Coincident(g6,g1)
    c: Block(g6)
    c: Coincident(g7,g5)
    c: Vertical(g7)
    c: Coincident(g8,g6)
    c: Block(g8)
    c: Block(g7)
    c: Coincident(g10,g9)
    c: Coincident(g10,g6)
    c: Horizontal(g10)
    c: Block(g10)
    c: Block(g9)
    c: Coincident(g11,g8)
    c: Horizontal(g11)
    c: Block(g12)
    c: Block(g11)
    c: Coincident(g13,g12)
    c: Coincident(g13,g9)
    c: Vertical(g13)
    c: Tangent(g13,g9)
FEATURE [Sketcher::SketchObject] Sketch047
  FullyConstrained = true
  MapMode = 4
  Placement = pos=(0,0,0) rot=(0.57735,0.57735,0.57735;2.0944rad)
  Support = -> [Cut014]
  sketch-geometry (14):
    g0: LineSegment StartX=6.08745 StartY=-4.11588 StartZ=0 EndX=6.08745 EndY=-2.11589 EndZ=0
    g1: LineSegment StartX=8.08745 StartY=1.38411 StartZ=0 EndX=8.08745 EndY=-1.11589 EndZ=0
    g2: ArcOfCircle CenterX=7.08745 CenterY=-1.11589 CenterZ=0 NormalX=0 NormalY=0 NormalZ=1 AngleXU=0 Radius=1 StartAngle=4.71239 EndAngle=6.28319
    g3: LineSegment StartX=6.08745 StartY=-2.11589 StartZ=0 EndX=7.08745 EndY=-2.11589 EndZ=0
    g4: LineSegment StartX=6.08745 StartY=-4.11588 StartZ=0 EndX=7.08745 EndY=-4.11588 EndZ=0
    g5: ArcOfCircle CenterX=7.08745 CenterY=-1.11589 CenterZ=0 NormalX=0 NormalY=0 NormalZ=1 AngleXU=0 Radius=3 StartAngle=4.71239 EndAngle=6.28319
    g6: ArcOfCircle CenterX=7.08745 CenterY=1.38411 CenterZ=0 NormalX=0 NormalY=0 NormalZ=1 AngleXU=0 Radius=1 StartAngle=5.35e-14 EndAngle=1.5708
    g7: LineSegment StartX=10.0875 StartY=-1.11588 StartZ=0 EndX=10.0875 EndY=1.38411 EndZ=0
    g8: ArcOfCircle CenterX=7.08745 CenterY=1.38411 CenterZ=0 NormalX=0 NormalY=0 NormalZ=1 AngleXU=0 Radius=3 StartAngle=3.57e-14 EndAngle=1.5708
    g9: ArcOfCircle CenterX=4.58745 CenterY=1.38412 CenterZ=0 NormalX=0 NormalY=0 NormalZ=1 AngleXU=0 Radius=1 StartAngle=1.57081 EndAngle=3.14159
    g10: LineSegment StartX=4.58744 StartY=2.38411 StartZ=0 EndX=7.08745 EndY=2.38411 EndZ=0
    g11: LineSegment StartX=4.58745 StartY=4.38411 StartZ=0 EndX=7.08745 EndY=4.38411 EndZ=0
    g12: ArcOfCircle CenterX=4.58745 CenterY=5.38411 CenterZ=0 NormalX=0 NormalY=0 NormalZ=1 AngleXU=0 Radius=1 StartAngle=3.14159 EndAngle=4.71239
    g13: LineSegment StartX=3.58745 StartY=5.38411 StartZ=0 EndX=3.58745 EndY=1.38411 EndZ=0
  constraints (33):
    c: Vertical(g0)
    c: Block(g0)
    c: Block(g1)
    c: Coincident(g2,g1)
    c: Coincident(g3,g0)
    c: Coincident(g3,g2)
    c: Horizontal(g3)
    c: Block(g2)
    c: Coincident(g4,g0)
    c: Horizontal(g4)
    c: Coincident(g5,g2)
    c: Block(g5)
    c: Block(g4)
    c: Coincident(g6,g1)
    c: Block(g6)
    c: Coincident(g7,g5)
    c: Vertical(g7)
    c: Coincident(g8,g6)
    c: Block(g8)
    c: Block(g7)
    c: Coincident(g10,g9)
    c: Coincident(g10,g6)
    c: Horizontal(g10)
    c: Block(g10)
    c: Block(g9)
    c: Coincident(g11,g8)
    c: Horizontal(g11)
    c: Block(g12)
    c: Block(g11)
    c: Coincident(g13,g12)
    c: Coincident(g13,g9)
    c: Vertical(g13)
    c: Tangent(g13,g9)
FEATURE [Sketcher::SketchObject] Sketch048
  FullyConstrained = true
  MapMode = 4
  Placement = pos=(0,0,0) rot=(0.57735,0.57735,0.57735;2.0944rad)
  Support = -> [Cut014]
  sketch-geometry (14):
    g0: LineSegment StartX=6.08745 StartY=-4.11588 StartZ=0 EndX=6.08745 EndY=-2.11589 EndZ=0
    g1: LineSegment StartX=8.08745 StartY=1.38411 StartZ=0 EndX=8.08745 EndY=-1.11589 EndZ=0
    g2: ArcOfCircle CenterX=7.08745 CenterY=-1.11589 CenterZ=0 NormalX=0 NormalY=0 NormalZ=1 AngleXU=0 Radius=1 StartAngle=4.71239 EndAngle=6.28319
    g3: LineSegment StartX=6.08745 StartY=-2.11589 StartZ=0 EndX=7.08745 EndY=-2.11589 EndZ=0
    g4: LineSegment StartX=6.08745 StartY=-4.11588 StartZ=0 EndX=7.08745 EndY=-4.11588 EndZ=0
    g5: ArcOfCircle CenterX=7.08745 CenterY=-1.11589 CenterZ=0 NormalX=0 NormalY=0 NormalZ=1 AngleXU=0 Radius=3 StartAngle=4.71239 EndAngle=6.28319
    g6: ArcOfCircle CenterX=7.08745 CenterY=1.38411 CenterZ=0 NormalX=0 NormalY=0 NormalZ=1 AngleXU=0 Radius=1 StartAngle=5.35e-14 EndAngle=1.5708
    g7: LineSegment StartX=10.0875 StartY=-1.11588 StartZ=0 EndX=10.0875 EndY=1.38411 EndZ=0
    g8: ArcOfCircle CenterX=7.08745 CenterY=1.38411 CenterZ=0 NormalX=0 NormalY=0 NormalZ=1 AngleXU=0 Radius=3 StartAngle=3.57e-14 EndAngle=1.5708
    g9: ArcOfCircle CenterX=4.58745 CenterY=1.38412 CenterZ=0 NormalX=0 NormalY=0 NormalZ=1 AngleXU=0 Radius=1 StartAngle=1.57081 EndAngle=3.14159
    g10: LineSegment StartX=4.58744 StartY=2.38411 StartZ=0 EndX=7.08745 EndY=2.38411 EndZ=0
    g11: LineSegment StartX=4.58745 StartY=4.38411 StartZ=0 EndX=7.08745 EndY=4.38411 EndZ=0
    g12: ArcOfCircle CenterX=4.58745 CenterY=5.38411 CenterZ=0 NormalX=0 NormalY=0 NormalZ=1 AngleXU=0 Radius=1 StartAngle=3.14159 EndAngle=4.71239
    g13: LineSegment StartX=3.58745 StartY=5.38411 StartZ=0 EndX=3.58745 EndY=1.38411 EndZ=0
  constraints (33):
    c: Vertical(g0)
    c: Block(g0)
    c: Block(g1)
    c: Coincident(g2,g1)
    c: Coincident(g3,g0)
    c: Coincident(g3,g2)
    c: Horizontal(g3)
    c: Block(g2)
    c: Coincident(g4,g0)
    c: Horizontal(g4)
    c: Coincident(g5,g2)
    c: Block(g5)
    c: Block(g4)
    c: Coincident(g6,g1)
    c: Block(g6)
    c: Coincident(g7,g5)
    c: Vertical(g7)
    c: Coincident(g8,g6)
    c: Block(g8)
    c: Block(g7)
    c: Coincident(g10,g9)
    c: Coincident(g10,g6)
    c: Horizontal(g10)
    c: Block(g10)
    c: Block(g9)
    c: Coincident(g11,g8)
    c: Horizontal(g11)
    c: Block(g12)
    c: Block(g11)
    c: Coincident(g13,g12)
    c: Coincident(g13,g9)
    c: Vertical(g13)
    c: Tangent(g13,g9)
FEATURE [Sketcher::SketchObject] Sketch049
  FullyConstrained = true
  MapMode = 4
  Placement = pos=(0,0,0) rot=(0.57735,0.57735,0.57735;2.0944rad)
  Support = -> [Cut014]
  sketch-geometry (14):
    g0: LineSegment StartX=6.08745 StartY=-4.11588 StartZ=0 EndX=6.08745 EndY=-2.11589 EndZ=0
    g1: LineSegment StartX=8.08745 StartY=1.38411 StartZ=0 EndX=8.08745 EndY=-1.11589 EndZ=0
    g2: ArcOfCircle CenterX=7.08745 CenterY=-1.11589 CenterZ=0 NormalX=0 NormalY=0 NormalZ=1 AngleXU=0 Radius=1 StartAngle=4.71239 EndAngle=6.28319
    g3: LineSegment StartX=6.08745 StartY=-2.11589 StartZ=0 EndX=7.08745 EndY=-2.11589 EndZ=0
    g4: LineSegment StartX=6.08745 StartY=-4.11588 StartZ=0 EndX=7.08745 EndY=-4.11588 EndZ=0
    g5: ArcOfCircle CenterX=7.08745 CenterY=-1.11589 CenterZ=0 NormalX=0 NormalY=0 NormalZ=1 AngleXU=0 Radius=3 StartAngle=4.71239 EndAngle=6.28319
    g6: ArcOfCircle CenterX=7.08745 CenterY=1.38411 CenterZ=0 NormalX=0 NormalY=0 NormalZ=1 AngleXU=0 Radius=1 StartAngle=5.35e-14 EndAngle=1.5708
    g7: LineSegment StartX=10.0875 StartY=-1.11588 StartZ=0 EndX=10.0875 EndY=1.38411 EndZ=0
    g8: ArcOfCircle CenterX=7.08745 CenterY=1.38411 CenterZ=0 NormalX=0 NormalY=0 NormalZ=1 AngleXU=0 Radius=3 StartAngle=3.57e-14 EndAngle=1.5708
    g9: ArcOfCircle CenterX=4.58745 CenterY=1.38412 CenterZ=0 NormalX=0 NormalY=0 NormalZ=1 AngleXU=0 Radius=1 StartAngle=1.57081 EndAngle=3.14159
    g10: LineSegment StartX=4.58744 StartY=2.38411 StartZ=0 EndX=7.08745 EndY=2.38411 EndZ=0
    g11: LineSegment StartX=4.58745 StartY=4.38411 StartZ=0 EndX=7.08745 EndY=4.38411 EndZ=0
    g12: ArcOfCircle CenterX=4.58745 CenterY=5.38411 CenterZ=0 NormalX=0 NormalY=0 NormalZ=1 AngleXU=0 Radius=1 StartAngle=3.14159 EndAngle=4.71239
    g13: LineSegment StartX=3.58745 StartY=5.38411 StartZ=0 EndX=3.58745 EndY=1.38411 EndZ=0
  constraints (33):
    c: Vertical(g0)
    c: Block(g0)
    c: Block(g1)
    c: Coincident(g2,g1)
    c: Coincident(g3,g0)
    c: Coincident(g3,g2)
    c: Horizontal(g3)
    c: Block(g2)
    c: Coincident(g4,g0)
    c: Horizontal(g4)
    c: Coincident(g5,g2)
    c: Block(g5)
    c: Block(g4)
    c: Coincident(g6,g1)
    c: Block(g6)
    c: Coincident(g7,g5)
    c: Vertical(g7)
    c: Coincident(g8,g6)
    c: Block(g8)
    c: Block(g7)
    c: Coincident(g10,g9)
    c: Coincident(g10,g6)
    c: Horizontal(g10)
    c: Block(g10)
    c: Block(g9)
    c: Coincident(g11,g8)
    c: Horizontal(g11)
    c: Block(g12)
    c: Block(g11)
    c: Coincident(g13,g12)
    c: Coincident(g13,g9)
    c: Vertical(g13)
    c: Tangent(g13,g9)
FEATURE [Part::Extrusion] Extrude041
  Base = -> Sketch049
  Dir = (1,0,0)
  DirMode = 2
  FaceMakerClass = Part::FaceMakerBullseye
  LengthFwd = 10
  LengthRev = 0
  Placement = pos=(-2,-22.615,14.6) rot=(0,0,1;3.14159rad)
  Solid = true
  Symmetric = false
FEATURE [Part::MultiFuse] Fusion023
  Shapes = -> [Extrude039,Extrude040,Extrude041,Cut014,Fusion015]
FEATURE [Part::Extrusion] Extrude042
  Base = -> Sketch034
  Dir = (0,0.894389,-0.447291)
  DirMode = 2
  FaceMakerClass = Part::FaceMakerBullseye
  LengthFwd = 14
  LengthRev = 0
  Placement = pos=(45.5,-14,11) rot=(1,0,0;0.466003rad)
  Solid = true
  Symmetric = false
FEATURE [Part::Fillet] Fillet021
  Base = -> Extrude042
  Edges = 1 edges r=1.95: [Edge2]
FEATURE [Part::Fillet] Fillet022
  Base = -> Fillet021
  Edges = 1 edges r=1.9: [Edge12]
  Placement = pos=(0,0,0.6) rot=(0,0,1;0rad)
FEATURE [Part::Box] Box014  label="Cube014"
  AttacherType = Attacher::AttachEngine3D
  Height = 2
  Length = 2
  Placement = pos=(-12.85,-28.2,0) rot=(0,0,1;0rad)
  Width = 2
FEATURE [App::MeasureDistance] Distance005  label="Distance: 15.50 mm"
  Distance = 15.5
  P1 = (-17.5,-32.7025,2.99911)
  P2 = (-2,-32.7025,2.99911)
FEATURE [Part::Box] Box015  label="Cube015"
  AttacherType = Attacher::AttachEngine3D
  Height = 2
  Length = 2
  Placement = pos=(-10.85,-28.2,0) rot=(0,0,1;0rad)
  Width = 2
FEATURE [Part::MultiFuse] Fusion024  label="wireHoldersecondery024"
  Placement = pos=(-8.65,0,10.48) rot=(0,0,1;0rad)
  Shapes = -> [Box015,Box014]
FEATURE [App::MeasureDistance] Distance006  label="Distance: 9.44 mm"
  Distance = 9.44274
  P1 = (-8.85,-28.2,0)
  P2 = (-2,-28.1337,6.49911)
FEATURE [Part::Box] Box016  label="Cube016"
  AttacherType = Attacher::AttachEngine3D
  Height = 2
  Length = 2
  Placement = pos=(-12.85,-28.2,0) rot=(0,0,1;0rad)
  Width = 2
FEATURE [Part::Box] Box017  label="Cube017"
  AttacherType = Attacher::AttachEngine3D
  Height = 2
  Length = 2
  Placement = pos=(-10.85,-28.2,0) rot=(0,0,1;0rad)
  Width = 2
FEATURE [Part::MultiFuse] Fusion025  label="wireHoldersecondery025"
  Placement = pos=(1,0,0) rot=(0,0,1;0rad)
  Shapes = -> [Box017,Box016]
FEATURE [App::MeasureDistance] Distance007  label="Distance: 1.58 mm"
  Distance = 1.582
  P1 = (-12,-28.7025,10.4841)
  P2 = (-13.5,-28.2,10.5)
FEATURE [App::MeasureDistance] Distance008  label="Distance: 1.58 mm001"
  Distance = 1.58193
  P1 = (-13.5,-28.2,10.49)
  P2 = (-12,-28.7025,10.4841)
FEATURE [App::MeasureDistance] Distance009  label="Distance: 1.58 mm002"
  Distance = 1.58192
  P1 = (-13.5,-28.2,10.48)
  P2 = (-12,-28.7025,10.4841)
FEATURE [Part::MultiFuse] Fusion026
  Shapes = -> [Fillet022,Fusion025,Fusion024,Fusion023]
